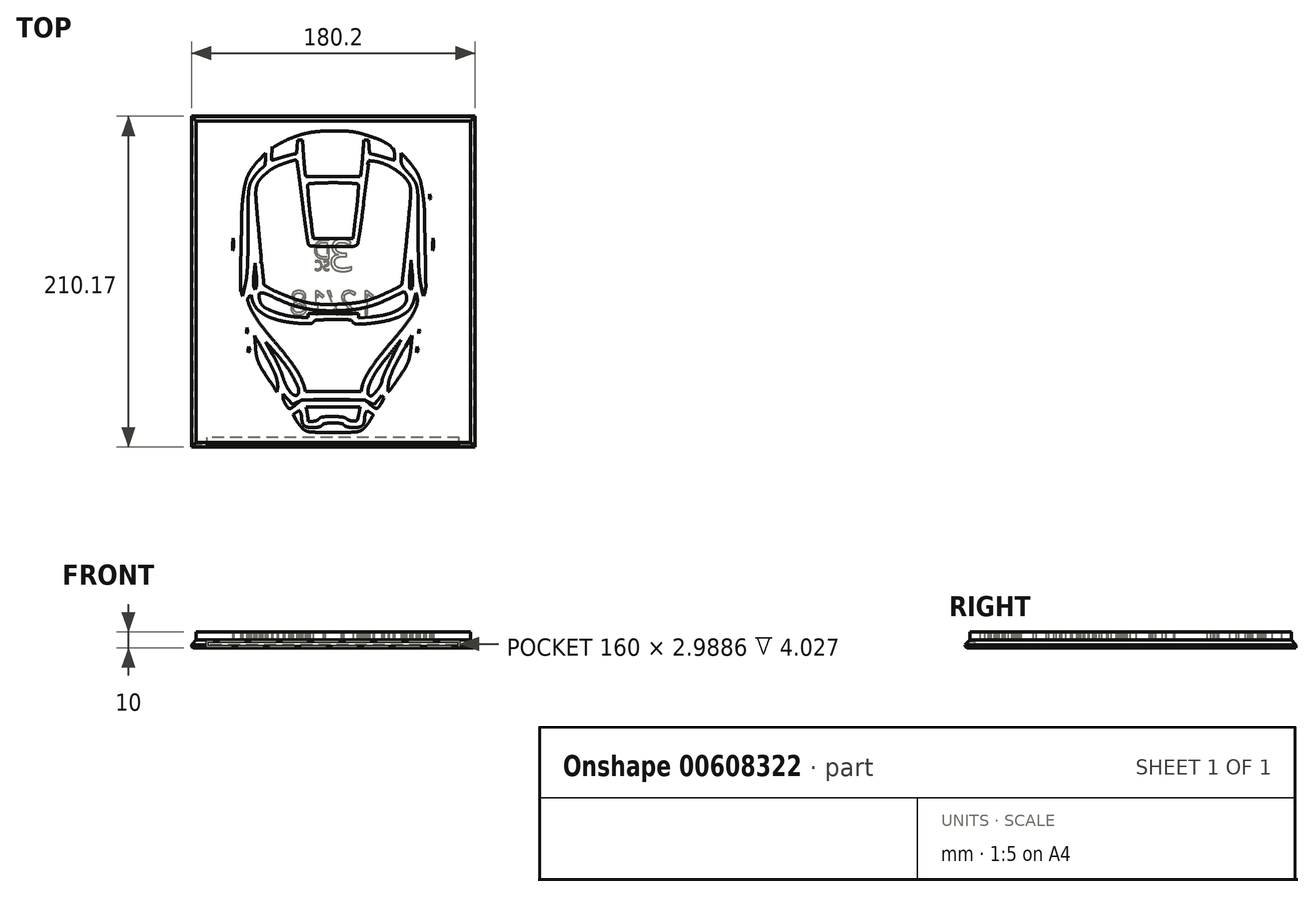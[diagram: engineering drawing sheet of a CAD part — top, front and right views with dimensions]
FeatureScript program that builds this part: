
annotation { "Feature Type Name" : "Feature", "Feature Type Description" : "" }
export const myFeature = defineFeature(function(context is Context, id is Id, definition is map)
    precondition{}
    {
        {
            var Q0;
            Q0=qCreatedBy(makeId("Top.planeOp"),FACE);
            var sketch = newSketch(context, id + "F0", { "sketchPlane" : qUnion([Q0])});
            skLineSegment(sketch, "E0.bottom", {"start": v(-90, 105) * mm, "end": v(90, 105) * mm});
            skLineSegment(sketch, "E0.top", {"start": v(-90, -105) * mm, "end": v(90, -105) * mm});
            skLineSegment(sketch, "E0.left", {"start": v(-90, 105) * mm, "end": v(-90, -105) * mm});
            skLineSegment(sketch, "E0.right", {"start": v(90, 105) * mm, "end": v(90, -105) * mm});
            skSolve(sketch);
        }
        {
            var Q0;
            Q0=makeQuery(id+"F0.imprint","IMPRINT",FACE,{"disambiguationData":[TD([[makeQuery(id+"F0.imprint","IMPRINT",EDGE,{"derivedFrom":sQuery(id+"F0.wireOp",EDGE,"E0.bottom")}),-1.0]])]});
            extrude(context, id + "F1", {"entities" : qUnion([Q0]), "depth" : 5 * mm, "offsetDistance" : 25 * mm, "hasDraft" : true, "draftAngle" : 3 * degree});
        }
        {
            var Q0;
            Q0=makeQuery(id+"F1.opExtrude","CAP_EDGE",EDGE,{"disambiguationData":[OSD([sQuery(id+"F0.wireOp",EDGE,"E0.left")])],"isStart":false});
            var Q1;
            Q1=makeQuery(id+"F1.opExtrude","CAP_EDGE",EDGE,{"disambiguationData":[OSD([sQuery(id+"F0.wireOp",EDGE,"E0.bottom")])],"isStart":false});
            var Q2;
            Q2=makeQuery(id+"F1.opExtrude","CAP_EDGE",EDGE,{"disambiguationData":[OSD([sQuery(id+"F0.wireOp",EDGE,"E0.right")])],"isStart":false});
            var Q3;
            Q3=makeQuery(id+"F1.opExtrude","CAP_EDGE",EDGE,{"disambiguationData":[OSD([sQuery(id+"F0.wireOp",EDGE,"E0.top")])],"isStart":false});
            chamfer(context, id + "F2", {"entities" : qUnion([Q0, Q1, Q2, Q3]), "width" : 3 * mm, "tangentPropagation" : true});
        }
        {
            var Q0;
            Q0=makeQuery(id+"F1.opExtrude","CAP_EDGE",EDGE,{"disambiguationData":[OSD([sQuery(id+"F0.wireOp",EDGE,"E0.right")])],"isStart":true});
            var Q1;
            {var subQ0=sQuery(id+"F0.wireOp",EDGE,"E0.bottom");Q1=makeQuery(id+"F2.opChamfer","BLEND_EDGE",EDGE,{"blendedFrom":[makeQuery(id+"F1.opExtrude","CAP_EDGE",EDGE,{"disambiguationData":[OSD([subQ0])],"isStart":false}),makeQuery(id+"F1.opExtrude","SWEPT_FACE",FACE,{"disambiguationData":[OSD([subQ0])]})],"blendedInto":[makeQuery(id+"F1.opExtrude","SWEPT_FACE",FACE,{"disambiguationData":[OSD([subQ0])]})]});}
            var Q2;
            Q2=makeQuery(id+"F1.opExtrude","CAP_EDGE",EDGE,{"disambiguationData":[OSD([sQuery(id+"F0.wireOp",EDGE,"E0.left")])],"isStart":true});
            var Q3;
            Q3=makeQuery(id+"F1.opExtrude","CAP_EDGE",EDGE,{"disambiguationData":[OSD([sQuery(id+"F0.wireOp",EDGE,"E0.top")])],"isStart":true});
            chamfer(context, id + "F3", {"entities" : qUnion([Q0, Q1, Q2, Q3]), "width" : 1 * mm, "tangentPropagation" : true});
        }
        {
            var Q0;
            Q0=makeQuery(id+"F1.opExtrude","CAP_FACE",FACE,{"disambiguationData":[OSD([sQuery(id+"F0.wireOp",EDGE,"E0.bottom"),sQuery(id+"F0.wireOp",EDGE,"E0.top"),sQuery(id+"F0.wireOp",EDGE,"E0.left"),sQuery(id+"F0.wireOp",EDGE,"E0.right")])],"isStart":true});
            var sketch = newSketch(context, id + "F4", { "sketchPlane" : qUnion([Q0])});
            skText(sketch, "E1", { "text": "D", "fontName": "OpenSans-Regular.ttf"});
            skText(sketch, "E2", { "text": "S", "fontName": "OpenSans-Regular.ttf"});
            skLineSegment(sketch, "E3", {"start": v(17.22, -16.7) * mm, "end": v(-3.14, -16.7) * mm, "construction": true});
            skText(sketch, "E4", { "text": "3", "fontName": "OpenSans-Regular.ttf"});
            skText(sketch, "E5", { "text": "C", "fontName": "OpenSans-Regular.ttf"});
            skText(sketch, "E6", { "text": "12/18", "fontName": "OpenSans-Regular.ttf"});
            const initialGuessF4  = {"E1": [-0.001, -0.01442, -1, 0, 0.0118], "E2": [-0.00213, -0.0072, -1, 0, 0.006], "E4": [0.01283, -0.0067, -1, 0, 0.02], "E5": [-0.00664, -0.0072, -1, 0, 0.006], "E6": [0.02743, 0.0209, -1, 0, 0.015]};
            skSetInitialGuess(sketch, initialGuessF4);
            skSolve(sketch);
        }
        {
            var Q0;
            Q0 = qSketchRegion(id + "F4", true);
            extrude(context, id + "F5", {"entities" : qUnion([Q0]), "operationType" : NewBodyOperationType.REMOVE, "flatOperationType" : FlatOperationType.REMOVE, "oppositeDirection" : true, "depth" : 0.5 * mm, "offsetDistance" : 25 * mm, "domain" : OperationDomain.MODEL});
        }
        {
            var Q0;
            Q0=makeQuery(id+"F1.opExtrude","CAP_FACE",FACE,{"disambiguationData":[OSD([sQuery(id+"F0.wireOp",EDGE,"E0.bottom"),sQuery(id+"F0.wireOp",EDGE,"E0.top"),sQuery(id+"F0.wireOp",EDGE,"E0.left"),sQuery(id+"F0.wireOp",EDGE,"E0.right")])],"isStart":false});
            var sketch = newSketch(context, id + "F6", { "sketchPlane" : qUnion([Q0])});
            skArc(sketch, "E7", {"start": v(-19.82, -98.53) * mm, "mid": v(-21.11, -97.69) * mm, "end": v(-22.15, -96.55) * mm});
            skArc(sketch, "E8", {"start": v(-22.15, -96.55) * mm, "mid": v(-28.55, -87.41) * mm, "end": v(-34.94, -78.26) * mm});
            skArc(sketch, "E9", {"start": v(-34.94, -78.26) * mm, "mid": v(-40.82, -69.73) * mm, "end": v(-46.64, -61.17) * mm});
            skArc(sketch, "E10", {"start": v(-46.64, -61.17) * mm, "mid": v(-49.1, -57.28) * mm, "end": v(-51.3, -53.25) * mm});
            skArc(sketch, "E11", {"start": v(-51.3, -53.25) * mm, "mid": v(-51.72, -52.27) * mm, "end": v(-52, -51.23) * mm});
            skArc(sketch, "E12", {"start": v(-52, -51.23) * mm, "mid": v(-52.4, -49.18) * mm, "end": v(-52.74, -47.12) * mm});
            skArc(sketch, "E13", {"start": v(-52.74, -47.12) * mm, "mid": v(-53.12, -44.5) * mm, "end": v(-53.44, -41.9) * mm});
            skArc(sketch, "E14", {"start": v(-53.44, -41.9) * mm, "mid": v(-53.76, -38.83) * mm, "end": v(-54.03, -35.75) * mm});
            skArc(sketch, "E15", {"start": v(-54.03, -35.75) * mm, "mid": v(-54.3, -32.88) * mm, "end": v(-54.6, -30.02) * mm});
            skArc(sketch, "E16", {"start": v(-54.6, -30.02) * mm, "mid": v(-54.9, -27.4) * mm, "end": v(-55.27, -24.78) * mm});
            skArc(sketch, "E17", {"start": v(-55.27, -24.78) * mm, "mid": v(-55.6, -22.6) * mm, "end": v(-55.98, -20.43) * mm});
            skArc(sketch, "E18", {"start": v(-55.98, -20.43) * mm, "mid": v(-56.2, -19.57) * mm, "end": v(-56.55, -18.75) * mm});
            skArc(sketch, "E19", {"start": v(-56.55, -18.75) * mm, "mid": v(-56.9, -18.1) * mm, "end": v(-57.23, -17.46) * mm});
            skArc(sketch, "E20", {"start": v(-57.23, -17.46) * mm, "mid": v(-57.75, -16.49) * mm, "end": v(-58.27, -15.52) * mm});
            skArc(sketch, "E21", {"start": v(-58.27, -15.52) * mm, "mid": v(-58.85, -14.44) * mm, "end": v(-59.43, -13.35) * mm});
            skArc(sketch, "E22", {"start": v(-59.43, -13.35) * mm, "mid": v(-60, -12.3) * mm, "end": v(-60.56, -11.25) * mm});
            skArc(sketch, "E23", {"start": v(-60.56, -11.25) * mm, "mid": v(-61.46, -9.37) * mm, "end": v(-62.14, -7.4) * mm});
            skArc(sketch, "E24", {"start": v(-62.14, -7.4) * mm, "mid": v(-62.6, -5.37) * mm, "end": v(-62.85, -3.32) * mm});
            skArc(sketch, "E25", {"start": v(-62.85, -3.32) * mm, "mid": v(-62.99, 0.04) * mm, "end": v(-63, 3.4) * mm});
            skArc(sketch, "E26", {"start": v(-63, 3.4) * mm, "mid": v(-62.83, 12.82) * mm, "end": v(-62.63, 22.25) * mm});
            skArc(sketch, "E27", {"start": v(-62.63, 22.25) * mm, "mid": v(-62.36, 32.9) * mm, "end": v(-62, 43.55) * mm});
            skArc(sketch, "E28", {"start": v(-62, 43.55) * mm, "mid": v(-61.67, 49.6) * mm, "end": v(-61.11, 55.62) * mm});
            skArc(sketch, "E29", {"start": v(-61.11, 55.62) * mm, "mid": v(-60.53, 59.69) * mm, "end": v(-59.7, 63.71) * mm});
            skArc(sketch, "E30", {"start": v(-59.7, 63.71) * mm, "mid": v(-58.7, 67.02) * mm, "end": v(-57.37, 70.2) * mm});
            skArc(sketch, "E31", {"start": v(-57.37, 70.2) * mm, "mid": v(-55.63, 73.3) * mm, "end": v(-53.57, 76.2) * mm});
            skArc(sketch, "E32", {"start": v(-53.57, 76.2) * mm, "mid": v(-50.88, 79.31) * mm, "end": v(-47.97, 82.23) * mm});
            skArc(sketch, "E33", {"start": v(-47.97, 82.23) * mm, "mid": v(-44.7, 85.08) * mm, "end": v(-41.22, 87.7) * mm});
            skArc(sketch, "E34", {"start": v(-41.22, 87.7) * mm, "mid": v(-37.66, 90.02) * mm, "end": v(-33.93, 92.06) * mm});
            skArc(sketch, "E35", {"start": v(-33.93, 92.06) * mm, "mid": v(-29.7, 94.07) * mm, "end": v(-25.37, 95.89) * mm});
            skArc(sketch, "E36", {"start": v(-25.37, 95.89) * mm, "mid": v(-21.73, 97.17) * mm, "end": v(-18, 98.16) * mm});
            skArc(sketch, "E37", {"start": v(-18, 98.16) * mm, "mid": v(-14.09, 98.9) * mm, "end": v(-10.14, 99.33) * mm});
            skArc(sketch, "E38", {"start": v(-10.14, 99.33) * mm, "mid": v(-5.1, 99.6) * mm, "end": v(-0.06, 99.7) * mm});
            skArc(sketch, "E39", {"start": v(-0.06, 99.7) * mm, "mid": v(4.99, 99.6) * mm, "end": v(10.03, 99.33) * mm});
            skArc(sketch, "E40", {"start": v(10.03, 99.33) * mm, "mid": v(13.97, 98.9) * mm, "end": v(17.88, 98.16) * mm});
            skArc(sketch, "E41", {"start": v(17.88, 98.16) * mm, "mid": v(21.61, 97.17) * mm, "end": v(25.26, 95.89) * mm});
            skArc(sketch, "E42", {"start": v(25.26, 95.89) * mm, "mid": v(29.58, 94.07) * mm, "end": v(33.82, 92.06) * mm});
            skArc(sketch, "E43", {"start": v(33.82, 92.06) * mm, "mid": v(37.54, 90.02) * mm, "end": v(41.1, 87.71) * mm});
            skArc(sketch, "E44", {"start": v(41.1, 87.71) * mm, "mid": v(44.57, 85.09) * mm, "end": v(47.85, 82.23) * mm});
            skArc(sketch, "E45", {"start": v(47.85, 82.23) * mm, "mid": v(50.76, 79.32) * mm, "end": v(53.45, 76.2) * mm});
            skArc(sketch, "E46", {"start": v(53.45, 76.2) * mm, "mid": v(55.53, 73.3) * mm, "end": v(57.27, 70.2) * mm});
            skArc(sketch, "E47", {"start": v(57.27, 70.2) * mm, "mid": v(58.6, 67.01) * mm, "end": v(59.57, 63.7) * mm});
            skArc(sketch, "E48", {"start": v(59.57, 63.7) * mm, "mid": v(60.41, 59.49) * mm, "end": v(61, 55.23) * mm});
            skArc(sketch, "E49", {"start": v(61, 55.23) * mm, "mid": v(61.57, 48.95) * mm, "end": v(61.91, 42.65) * mm});
            skArc(sketch, "E50", {"start": v(61.91, 42.65) * mm, "mid": v(62.28, 31.97) * mm, "end": v(62.55, 21.28) * mm});
            skArc(sketch, "E51", {"start": v(62.55, 21.28) * mm, "mid": v(62.74, 12.18) * mm, "end": v(62.9, 3.07) * mm});
            skArc(sketch, "E52", {"start": v(62.9, 3.07) * mm, "mid": v(62.88, -0.18) * mm, "end": v(62.74, -3.44) * mm});
            skArc(sketch, "E53", {"start": v(62.74, -3.44) * mm, "mid": v(62.5, -5.45) * mm, "end": v(62.03, -7.42) * mm});
            skArc(sketch, "E54", {"start": v(62.03, -7.42) * mm, "mid": v(61.34, -9.38) * mm, "end": v(60.45, -11.25) * mm});
            skArc(sketch, "E55", {"start": v(60.45, -11.25) * mm, "mid": v(59.89, -12.3) * mm, "end": v(59.32, -13.35) * mm});
            skArc(sketch, "E56", {"start": v(59.32, -13.35) * mm, "mid": v(58.74, -14.44) * mm, "end": v(58.16, -15.52) * mm});
            skArc(sketch, "E57", {"start": v(58.16, -15.52) * mm, "mid": v(57.64, -16.49) * mm, "end": v(57.12, -17.46) * mm});
            skArc(sketch, "E58", {"start": v(57.12, -17.46) * mm, "mid": v(56.78, -18.1) * mm, "end": v(56.44, -18.75) * mm});
            skArc(sketch, "E59", {"start": v(56.44, -18.75) * mm, "mid": v(56.09, -19.57) * mm, "end": v(55.86, -20.43) * mm});
            skArc(sketch, "E60", {"start": v(55.86, -20.43) * mm, "mid": v(55.5, -22.6) * mm, "end": v(55.16, -24.78) * mm});
            skArc(sketch, "E61", {"start": v(55.16, -24.78) * mm, "mid": v(54.8, -27.4) * mm, "end": v(54.48, -30.02) * mm});
            skArc(sketch, "E62", {"start": v(54.48, -30.02) * mm, "mid": v(54.18, -32.88) * mm, "end": v(53.92, -35.75) * mm});
            skArc(sketch, "E63", {"start": v(53.92, -35.75) * mm, "mid": v(53.64, -38.83) * mm, "end": v(53.32, -41.9) * mm});
            skArc(sketch, "E64", {"start": v(53.32, -41.9) * mm, "mid": v(53, -44.5) * mm, "end": v(52.63, -47.12) * mm});
            skArc(sketch, "E65", {"start": v(52.63, -47.12) * mm, "mid": v(52.28, -49.18) * mm, "end": v(51.9, -51.23) * mm});
            skArc(sketch, "E66", {"start": v(51.9, -51.23) * mm, "mid": v(51.6, -52.27) * mm, "end": v(51.19, -53.25) * mm});
            skArc(sketch, "E67", {"start": v(51.19, -53.25) * mm, "mid": v(50.64, -54.26) * mm, "end": v(50.05, -55.24) * mm});
            skArc(sketch, "E68", {"start": v(50.05, -55.24) * mm, "mid": v(48.05, -58.33) * mm, "end": v(46.05, -61.42) * mm});
            skArc(sketch, "E69", {"start": v(46.05, -61.42) * mm, "mid": v(43.65, -65.08) * mm, "end": v(41.24, -68.73) * mm});
            skArc(sketch, "E70", {"start": v(41.24, -68.73) * mm, "mid": v(38.54, -72.79) * mm, "end": v(35.83, -76.83) * mm});
            skArc(sketch, "E71", {"start": v(35.83, -76.83) * mm, "mid": v(32.8, -81.28) * mm, "end": v(29.75, -85.71) * mm});
            skArc(sketch, "E72", {"start": v(29.75, -85.71) * mm, "mid": v(27.37, -89.06) * mm, "end": v(24.92, -92.37) * mm});
            skArc(sketch, "E73", {"start": v(24.92, -92.37) * mm, "mid": v(23.03, -94.84) * mm, "end": v(21.1, -97.28) * mm});
            skArc(sketch, "E74", {"start": v(21.1, -97.28) * mm, "mid": v(20.33, -98.03) * mm, "end": v(19.42, -98.58) * mm});
            skArc(sketch, "E75", {"start": v(19.42, -98.58) * mm, "mid": v(17.28, -99.3) * mm, "end": v(15.03, -99.58) * mm});
            skArc(sketch, "E76", {"start": v(15.03, -99.58) * mm, "mid": v(7.38, -99.68) * mm, "end": v(-0.26, -99.7) * mm});
            skArc(sketch, "E77", {"start": v(-0.26, -99.7) * mm, "mid": v(-7.93, -99.65) * mm, "end": v(-15.6, -99.54) * mm});
            skArc(sketch, "E78", {"start": v(-15.6, -99.54) * mm, "mid": v(-17.76, -99.26) * mm, "end": v(-19.82, -98.53) * mm});
            skArc(sketch, "E79", {"start": v(19.8, -92.91) * mm, "mid": v(20.36, -92.28) * mm, "end": v(20.92, -91.62) * mm});
            skArc(sketch, "E80", {"start": v(20.92, -91.62) * mm, "mid": v(21.52, -90.87) * mm, "end": v(22.1, -90.1) * mm});
            skArc(sketch, "E81", {"start": v(22.1, -90.1) * mm, "mid": v(22.64, -89.34) * mm, "end": v(23.16, -88.57) * mm});
            skArc(sketch, "E82", {"start": v(23.16, -88.57) * mm, "mid": v(24.32, -86.59) * mm, "end": v(25.39, -84.55) * mm});
            skLineSegment(sketch, "E83", {"start": v(25.39, -84.55) * mm, "end": v(23.48, -83.15) * mm});
            skLineSegment(sketch, "E84", {"start": v(23.48, -83.15) * mm, "end": v(21.56, -81.75) * mm});
            skLineSegment(sketch, "E85", {"start": v(21.56, -81.75) * mm, "end": v(20.77, -83) * mm});
            skArc(sketch, "E86", {"start": v(20.77, -83) * mm, "mid": v(20.6, -83.32) * mm, "end": v(20.46, -83.65) * mm});
            skArc(sketch, "E87", {"start": v(20.46, -83.65) * mm, "mid": v(20.32, -84.1) * mm, "end": v(20.2, -84.57) * mm});
            skArc(sketch, "E88", {"start": v(20.2, -84.57) * mm, "mid": v(20.1, -85.08) * mm, "end": v(20.02, -85.6) * mm});
            skArc(sketch, "E89", {"start": v(20.02, -85.6) * mm, "mid": v(19.98, -86.08) * mm, "end": v(19.96, -86.57) * mm});
            skArc(sketch, "E90", {"start": v(19.96, -86.57) * mm, "mid": v(19.86, -88.07) * mm, "end": v(19.57, -89.54) * mm});
            skArc(sketch, "E91", {"start": v(19.57, -89.54) * mm, "mid": v(19.14, -90.56) * mm, "end": v(18.44, -91.41) * mm});
            skArc(sketch, "E92", {"start": v(18.44, -91.41) * mm, "mid": v(17.47, -92.07) * mm, "end": v(16.37, -92.44) * mm});
            skArc(sketch, "E93", {"start": v(16.37, -92.44) * mm, "mid": v(14.7, -92.67) * mm, "end": v(13.03, -92.75) * mm});
            skArc(sketch, "E94", {"start": v(13.03, -92.75) * mm, "mid": v(11.96, -92.73) * mm, "end": v(10.9, -92.66) * mm});
            skArc(sketch, "E95", {"start": v(10.9, -92.66) * mm, "mid": v(10, -92.54) * mm, "end": v(9.13, -92.36) * mm});
            skArc(sketch, "E96", {"start": v(9.13, -92.36) * mm, "mid": v(8.44, -92.16) * mm, "end": v(7.78, -91.9) * mm});
            skArc(sketch, "E97", {"start": v(7.78, -91.9) * mm, "mid": v(7.32, -91.62) * mm, "end": v(6.94, -91.25) * mm});
            skArc(sketch, "E98", {"start": v(6.94, -91.25) * mm, "mid": v(6.54, -90.87) * mm, "end": v(6.05, -90.59) * mm});
            skArc(sketch, "E99", {"start": v(6.05, -90.59) * mm, "mid": v(5.33, -90.32) * mm, "end": v(4.59, -90.12) * mm});
            skArc(sketch, "E100", {"start": v(4.59, -90.12) * mm, "mid": v(3.59, -89.95) * mm, "end": v(2.58, -89.84) * mm});
            skArc(sketch, "E101", {"start": v(2.58, -89.84) * mm, "mid": v(1.26, -89.78) * mm, "end": v(-0.06, -89.75) * mm});
            skArc(sketch, "E102", {"start": v(-0.06, -89.75) * mm, "mid": v(-1.37, -89.78) * mm, "end": v(-2.7, -89.84) * mm});
            skArc(sketch, "E103", {"start": v(-2.7, -89.84) * mm, "mid": v(-3.7, -89.95) * mm, "end": v(-4.7, -90.12) * mm});
            skArc(sketch, "E104", {"start": v(-4.7, -90.12) * mm, "mid": v(-5.44, -90.32) * mm, "end": v(-6.16, -90.59) * mm});
            skArc(sketch, "E105", {"start": v(-6.16, -90.59) * mm, "mid": v(-6.65, -90.87) * mm, "end": v(-7.06, -91.25) * mm});
            skArc(sketch, "E106", {"start": v(-7.06, -91.25) * mm, "mid": v(-7.44, -91.62) * mm, "end": v(-7.9, -91.9) * mm});
            skArc(sketch, "E107", {"start": v(-7.9, -91.9) * mm, "mid": v(-8.55, -92.16) * mm, "end": v(-9.24, -92.36) * mm});
            skArc(sketch, "E108", {"start": v(-9.24, -92.36) * mm, "mid": v(-10.12, -92.54) * mm, "end": v(-11, -92.66) * mm});
            skArc(sketch, "E109", {"start": v(-11, -92.66) * mm, "mid": v(-12.07, -92.73) * mm, "end": v(-13.14, -92.75) * mm});
            skArc(sketch, "E110", {"start": v(-13.14, -92.75) * mm, "mid": v(-14.82, -92.67) * mm, "end": v(-16.48, -92.44) * mm});
            skArc(sketch, "E111", {"start": v(-16.48, -92.44) * mm, "mid": v(-17.58, -92.07) * mm, "end": v(-18.55, -91.41) * mm});
            skArc(sketch, "E112", {"start": v(-18.55, -91.41) * mm, "mid": v(-19.26, -90.56) * mm, "end": v(-19.69, -89.54) * mm});
            skArc(sketch, "E113", {"start": v(-19.69, -89.54) * mm, "mid": v(-19.97, -88.07) * mm, "end": v(-20.07, -86.57) * mm});
            skArc(sketch, "E114", {"start": v(-20.07, -86.57) * mm, "mid": v(-20.09, -86.08) * mm, "end": v(-20.14, -85.6) * mm});
            skArc(sketch, "E115", {"start": v(-20.14, -85.6) * mm, "mid": v(-20.21, -85.08) * mm, "end": v(-20.32, -84.57) * mm});
            skArc(sketch, "E116", {"start": v(-20.32, -84.57) * mm, "mid": v(-20.43, -84.1) * mm, "end": v(-20.57, -83.65) * mm});
            skArc(sketch, "E117", {"start": v(-20.57, -83.65) * mm, "mid": v(-21.07, -82.67) * mm, "end": v(-21.67, -81.75) * mm});
            skLineSegment(sketch, "E118", {"start": v(-21.67, -81.75) * mm, "end": v(-23.59, -83.15) * mm});
            skLineSegment(sketch, "E119", {"start": v(-23.59, -83.15) * mm, "end": v(-25.5, -84.55) * mm});
            skLineSegment(sketch, "E120", {"start": v(-25.5, -84.55) * mm, "end": v(-24.03, -87.31) * mm});
            skArc(sketch, "E121", {"start": v(-24.03, -87.31) * mm, "mid": v(-23.67, -87.95) * mm, "end": v(-23.28, -88.57) * mm});
            skArc(sketch, "E122", {"start": v(-23.28, -88.57) * mm, "mid": v(-22.75, -89.34) * mm, "end": v(-22.21, -90.1) * mm});
            skArc(sketch, "E123", {"start": v(-22.21, -90.1) * mm, "mid": v(-21.63, -90.87) * mm, "end": v(-21.03, -91.62) * mm});
            skArc(sketch, "E124", {"start": v(-21.03, -91.62) * mm, "mid": v(-20.48, -92.28) * mm, "end": v(-19.9, -92.91) * mm});
            skArc(sketch, "E125", {"start": v(-19.9, -92.91) * mm, "mid": v(-18.91, -93.83) * mm, "end": v(-17.8, -94.59) * mm});
            skArc(sketch, "E126", {"start": v(-17.8, -94.59) * mm, "mid": v(-16.65, -95.1) * mm, "end": v(-15.44, -95.4) * mm});
            skArc(sketch, "E127", {"start": v(-15.44, -95.4) * mm, "mid": v(-13.44, -95.62) * mm, "end": v(-11.43, -95.7) * mm});
            skArc(sketch, "E128", {"start": v(-11.43, -95.7) * mm, "mid": v(-5.75, -95.74) * mm, "end": v(-0.06, -95.75) * mm});
            skArc(sketch, "E129", {"start": v(-0.06, -95.75) * mm, "mid": v(5.63, -95.74) * mm, "end": v(11.32, -95.7) * mm});
            skArc(sketch, "E130", {"start": v(11.32, -95.7) * mm, "mid": v(13.33, -95.62) * mm, "end": v(15.32, -95.4) * mm});
            skArc(sketch, "E131", {"start": v(15.32, -95.4) * mm, "mid": v(16.54, -95.1) * mm, "end": v(17.68, -94.59) * mm});
            skArc(sketch, "E132", {"start": v(17.68, -94.59) * mm, "mid": v(18.8, -93.83) * mm, "end": v(19.8, -92.91) * mm});
            skArc(sketch, "E133", {"start": v(-9.06, -87.25) * mm, "mid": v(-8, -86.39) * mm, "end": v(-6.68, -86) * mm});
            skArc(sketch, "E134", {"start": v(-6.68, -86) * mm, "mid": v(-3.67, -85.77) * mm, "end": v(-0.65, -85.7) * mm});
            skArc(sketch, "E135", {"start": v(-0.65, -85.7) * mm, "mid": v(2.38, -85.77) * mm, "end": v(5.4, -86) * mm});
            skArc(sketch, "E136", {"start": v(5.4, -86) * mm, "mid": v(7.04, -86.4) * mm, "end": v(8.5, -87.22) * mm});
            skArc(sketch, "E137", {"start": v(8.5, -87.22) * mm, "mid": v(9.34, -87.76) * mm, "end": v(10.25, -88.17) * mm});
            skArc(sketch, "E138", {"start": v(10.25, -88.17) * mm, "mid": v(11.3, -88.48) * mm, "end": v(12.39, -88.67) * mm});
            skArc(sketch, "E139", {"start": v(12.39, -88.67) * mm, "mid": v(13.34, -88.72) * mm, "end": v(14.3, -88.65) * mm});
            skArc(sketch, "E140", {"start": v(14.3, -88.65) * mm, "mid": v(14.85, -88.44) * mm, "end": v(15.25, -88) * mm});
            skArc(sketch, "E141", {"start": v(15.25, -88) * mm, "mid": v(15.37, -87.77) * mm, "end": v(15.46, -87.52) * mm});
            skArc(sketch, "E142", {"start": v(15.46, -87.52) * mm, "mid": v(15.6, -86.95) * mm, "end": v(15.75, -86.37) * mm});
            skArc(sketch, "E143", {"start": v(15.75, -86.37) * mm, "mid": v(15.92, -85.69) * mm, "end": v(16.07, -85) * mm});
            skArc(sketch, "E144", {"start": v(16.07, -85) * mm, "mid": v(16.57, -82.38) * mm, "end": v(17.03, -79.75) * mm});
            skLineSegment(sketch, "E145", {"start": v(17.03, -79.75) * mm, "end": v(-0.14, -79.75) * mm});
            skLineSegment(sketch, "E146", {"start": v(-0.14, -79.75) * mm, "end": v(-17.3, -79.75) * mm});
            skLineSegment(sketch, "E147", {"start": v(-17.3, -79.75) * mm, "end": v(-16.68, -82.88) * mm});
            skArc(sketch, "E148", {"start": v(-16.68, -82.88) * mm, "mid": v(-16.56, -83.53) * mm, "end": v(-16.44, -84.18) * mm});
            skArc(sketch, "E149", {"start": v(-16.44, -84.18) * mm, "mid": v(-16.34, -84.83) * mm, "end": v(-16.24, -85.49) * mm});
            skArc(sketch, "E150", {"start": v(-16.24, -85.49) * mm, "mid": v(-16.16, -86.07) * mm, "end": v(-16.1, -86.65) * mm});
            skArc(sketch, "E151", {"start": v(-16.1, -86.65) * mm, "mid": v(-16.05, -87.7) * mm, "end": v(-16.06, -88.75) * mm});
            skLineSegment(sketch, "E152", {"start": v(-16.06, -88.75) * mm, "end": v(-13.18, -88.75) * mm});
            skArc(sketch, "E153", {"start": v(-13.18, -88.75) * mm, "mid": v(-12.58, -88.73) * mm, "end": v(-11.99, -88.64) * mm});
            skArc(sketch, "E154", {"start": v(-11.99, -88.64) * mm, "mid": v(-11.38, -88.5) * mm, "end": v(-10.78, -88.31) * mm});
            skArc(sketch, "E155", {"start": v(-10.78, -88.31) * mm, "mid": v(-10.25, -88.1) * mm, "end": v(-9.74, -87.83) * mm});
            skArc(sketch, "E156", {"start": v(-9.74, -87.83) * mm, "mid": v(-9.37, -87.57) * mm, "end": v(-9.06, -87.25) * mm});
            skLineSegment(sketch, "E157", {"start": v(-23.56, -78.17) * mm, "end": v(-20.56, -75.66) * mm});
            skLineSegment(sketch, "E158", {"start": v(-20.56, -75.66) * mm, "end": v(-23.21, -76.82) * mm});
            skLineSegment(sketch, "E159", {"start": v(-23.21, -76.82) * mm, "end": v(-25.87, -78) * mm});
            skLineSegment(sketch, "E160", {"start": v(-25.87, -78) * mm, "end": v(-28.94, -74.62) * mm});
            skLineSegment(sketch, "E161", {"start": v(-28.94, -74.62) * mm, "end": v(-32, -71.25) * mm});
            skLineSegment(sketch, "E162", {"start": v(-32, -71.25) * mm, "end": v(-32.03, -73.1) * mm});
            skArc(sketch, "E163", {"start": v(-32.03, -73.1) * mm, "mid": v(-31.94, -74.13) * mm, "end": v(-31.65, -75.13) * mm});
            skArc(sketch, "E164", {"start": v(-31.65, -75.13) * mm, "mid": v(-31.04, -76.5) * mm, "end": v(-30.34, -77.8) * mm});
            skArc(sketch, "E165", {"start": v(-30.34, -77.8) * mm, "mid": v(-29.58, -79.01) * mm, "end": v(-28.75, -80.17) * mm});
            skArc(sketch, "E166", {"start": v(-28.75, -80.17) * mm, "mid": v(-28.24, -80.58) * mm, "end": v(-27.6, -80.72) * mm});
            skArc(sketch, "E167", {"start": v(-27.6, -80.72) * mm, "mid": v(-27.3, -80.67) * mm, "end": v(-27.02, -80.56) * mm});
            skArc(sketch, "E168", {"start": v(-27.02, -80.56) * mm, "mid": v(-26.5, -80.27) * mm, "end": v(-25.98, -79.95) * mm});
            skArc(sketch, "E169", {"start": v(-25.98, -79.95) * mm, "mid": v(-25.37, -79.56) * mm, "end": v(-24.78, -79.13) * mm});
            skArc(sketch, "E170", {"start": v(-24.78, -79.13) * mm, "mid": v(-24.16, -78.66) * mm, "end": v(-23.56, -78.17) * mm});
            skLineSegment(sketch, "E171", {"start": v(30.5, -77.3) * mm, "end": v(32.36, -73.83) * mm});
            skLineSegment(sketch, "E172", {"start": v(32.36, -73.83) * mm, "end": v(31.56, -73.04) * mm});
            skLineSegment(sketch, "E173", {"start": v(31.56, -73.04) * mm, "end": v(30.77, -72.25) * mm});
            skLineSegment(sketch, "E174", {"start": v(30.77, -72.25) * mm, "end": v(28.3, -75.13) * mm});
            skLineSegment(sketch, "E175", {"start": v(28.3, -75.13) * mm, "end": v(25.81, -78.02) * mm});
            skLineSegment(sketch, "E176", {"start": v(25.81, -78.02) * mm, "end": v(23.13, -76.84) * mm});
            skLineSegment(sketch, "E177", {"start": v(23.13, -76.84) * mm, "end": v(20.44, -75.66) * mm});
            skLineSegment(sketch, "E178", {"start": v(20.44, -75.66) * mm, "end": v(23.44, -78.17) * mm});
            skArc(sketch, "E179", {"start": v(23.44, -78.17) * mm, "mid": v(24.73, -79.2) * mm, "end": v(26.08, -80.15) * mm});
            skArc(sketch, "E180", {"start": v(26.08, -80.15) * mm, "mid": v(26.82, -80.47) * mm, "end": v(27.63, -80.52) * mm});
            skArc(sketch, "E181", {"start": v(27.63, -80.52) * mm, "mid": v(28.36, -80.27) * mm, "end": v(28.93, -79.75) * mm});
            skArc(sketch, "E182", {"start": v(28.93, -79.75) * mm, "mid": v(29.76, -78.55) * mm, "end": v(30.5, -77.3) * mm});
            skArc(sketch, "E183", {"start": v(10.2, -75) * mm, "mid": v(7.86, -74.95) * mm, "end": v(5.53, -74.9) * mm});
            skArc(sketch, "E184", {"start": v(5.53, -74.9) * mm, "mid": v(2.74, -74.88) * mm, "end": v(-0.06, -74.87) * mm});
            skArc(sketch, "E185", {"start": v(-0.06, -74.87) * mm, "mid": v(-2.85, -74.88) * mm, "end": v(-5.64, -74.9) * mm});
            skArc(sketch, "E186", {"start": v(-5.64, -74.9) * mm, "mid": v(-13.1, -75.08) * mm, "end": v(-20.56, -75.33) * mm});
            skLineSegment(sketch, "E187", {"start": v(-20.56, -75.33) * mm, "end": v(-0.06, -75.33) * mm});
            skLineSegment(sketch, "E188", {"start": v(-0.06, -75.33) * mm, "end": v(20.44, -75.33) * mm});
            skLineSegment(sketch, "E189", {"start": v(20.44, -75.33) * mm, "end": v(10.2, -75) * mm});
            skArc(sketch, "E190", {"start": v(-22.52, -71.69) * mm, "mid": v(-21.9, -69.83) * mm, "end": v(-22.16, -67.89) * mm});
            skArc(sketch, "E191", {"start": v(-22.16, -67.89) * mm, "mid": v(-23.74, -64.2) * mm, "end": v(-25.56, -60.62) * mm});
            skArc(sketch, "E192", {"start": v(-25.56, -60.62) * mm, "mid": v(-28.13, -56.3) * mm, "end": v(-31, -52.18) * mm});
            skArc(sketch, "E193", {"start": v(-31, -52.18) * mm, "mid": v(-36.82, -45.06) * mm, "end": v(-43, -38.25) * mm});
            skLineSegment(sketch, "E194", {"start": v(-43, -38.25) * mm, "end": v(-38.5, -46.25) * mm});
            skArc(sketch, "E195", {"start": v(-38.5, -46.25) * mm, "mid": v(-37.57, -47.98) * mm, "end": v(-36.66, -49.72) * mm});
            skArc(sketch, "E196", {"start": v(-36.66, -49.72) * mm, "mid": v(-35.73, -51.61) * mm, "end": v(-34.84, -53.52) * mm});
            skArc(sketch, "E197", {"start": v(-34.84, -53.52) * mm, "mid": v(-34.05, -55.3) * mm, "end": v(-33.29, -57.09) * mm});
            skArc(sketch, "E198", {"start": v(-33.29, -57.09) * mm, "mid": v(-32.78, -58.41) * mm, "end": v(-32.34, -59.75) * mm});
            skArc(sketch, "E199", {"start": v(-32.34, -59.75) * mm, "mid": v(-31.28, -62.8) * mm, "end": v(-30.01, -65.78) * mm});
            skArc(sketch, "E200", {"start": v(-30.01, -65.78) * mm, "mid": v(-28.72, -68.13) * mm, "end": v(-27.15, -70.3) * mm});
            skArc(sketch, "E201", {"start": v(-27.15, -70.3) * mm, "mid": v(-25.94, -71.47) * mm, "end": v(-24.49, -72.3) * mm});
            skArc(sketch, "E202", {"start": v(-24.49, -72.3) * mm, "mid": v(-23.39, -72.37) * mm, "end": v(-22.52, -71.69) * mm});
            skArc(sketch, "E203", {"start": v(27.87, -69.03) * mm, "mid": v(28.48, -68.24) * mm, "end": v(29.05, -67.43) * mm});
            skArc(sketch, "E204", {"start": v(29.05, -67.43) * mm, "mid": v(29.57, -66.6) * mm, "end": v(30.04, -65.72) * mm});
            skArc(sketch, "E205", {"start": v(30.04, -65.72) * mm, "mid": v(30.41, -64.94) * mm, "end": v(30.74, -64.15) * mm});
            skArc(sketch, "E206", {"start": v(30.74, -64.15) * mm, "mid": v(30.9, -63.6) * mm, "end": v(30.94, -63.02) * mm});
            skArc(sketch, "E207", {"start": v(30.94, -63.02) * mm, "mid": v(31.01, -62.29) * mm, "end": v(31.22, -61.59) * mm});
            skArc(sketch, "E208", {"start": v(31.22, -61.59) * mm, "mid": v(31.95, -59.77) * mm, "end": v(32.7, -57.96) * mm});
            skArc(sketch, "E209", {"start": v(32.7, -57.96) * mm, "mid": v(33.66, -55.8) * mm, "end": v(34.65, -53.66) * mm});
            skArc(sketch, "E210", {"start": v(34.65, -53.66) * mm, "mid": v(38.74, -45.43) * mm, "end": v(42.95, -37.25) * mm});
            skLineSegment(sketch, "E211", {"start": v(42.95, -37.25) * mm, "end": v(41.2, -39.37) * mm});
            skArc(sketch, "E212", {"start": v(41.2, -39.37) * mm, "mid": v(37.74, -43.56) * mm, "end": v(34.31, -47.77) * mm});
            skArc(sketch, "E213", {"start": v(34.31, -47.77) * mm, "mid": v(32.2, -50.44) * mm, "end": v(30.12, -53.16) * mm});
            skArc(sketch, "E214", {"start": v(30.12, -53.16) * mm, "mid": v(28.66, -55.2) * mm, "end": v(27.26, -57.28) * mm});
            skArc(sketch, "E215", {"start": v(27.26, -57.28) * mm, "mid": v(26.09, -59.19) * mm, "end": v(25, -61.15) * mm});
            skArc(sketch, "E216", {"start": v(25, -61.15) * mm, "mid": v(24.05, -63.06) * mm, "end": v(23.18, -65.01) * mm});
            skArc(sketch, "E217", {"start": v(23.18, -65.01) * mm, "mid": v(22.6, -66.57) * mm, "end": v(22.17, -68.18) * mm});
            skArc(sketch, "E218", {"start": v(22.17, -68.18) * mm, "mid": v(22, -69.38) * mm, "end": v(21.96, -70.6) * mm});
            skArc(sketch, "E219", {"start": v(21.96, -70.6) * mm, "mid": v(22.14, -71.4) * mm, "end": v(22.61, -72.09) * mm});
            skArc(sketch, "E220", {"start": v(22.61, -72.09) * mm, "mid": v(23.05, -72.4) * mm, "end": v(23.56, -72.6) * mm});
            skArc(sketch, "E221", {"start": v(23.56, -72.6) * mm, "mid": v(24.07, -72.6) * mm, "end": v(24.54, -72.42) * mm});
            skArc(sketch, "E222", {"start": v(24.54, -72.42) * mm, "mid": v(25.22, -71.96) * mm, "end": v(25.8, -71.4) * mm});
            skArc(sketch, "E223", {"start": v(25.8, -71.4) * mm, "mid": v(26.85, -70.23) * mm, "end": v(27.87, -69.03) * mm});
            skArc(sketch, "E224", {"start": v(-36.5, -59.97) * mm, "mid": v(-36.96, -58.71) * mm, "end": v(-37.5, -57.48) * mm});
            skArc(sketch, "E225", {"start": v(-37.5, -57.48) * mm, "mid": v(-38.43, -55.51) * mm, "end": v(-39.39, -53.56) * mm});
            skArc(sketch, "E226", {"start": v(-39.39, -53.56) * mm, "mid": v(-40.52, -51.33) * mm, "end": v(-41.68, -49.12) * mm});
            skArc(sketch, "E227", {"start": v(-41.68, -49.12) * mm, "mid": v(-45.85, -41.66) * mm, "end": v(-50.13, -34.25) * mm});
            skLineSegment(sketch, "E228", {"start": v(-50.13, -34.25) * mm, "end": v(-49.46, -41.75) * mm});
            skArc(sketch, "E229", {"start": v(-49.46, -41.75) * mm, "mid": v(-49.14, -44.57) * mm, "end": v(-48.7, -47.37) * mm});
            skArc(sketch, "E230", {"start": v(-48.7, -47.37) * mm, "mid": v(-48.2, -49.43) * mm, "end": v(-47.5, -51.42) * mm});
            skArc(sketch, "E231", {"start": v(-47.5, -51.42) * mm, "mid": v(-46.46, -53.63) * mm, "end": v(-45.25, -55.74) * mm});
            skArc(sketch, "E232", {"start": v(-45.25, -55.74) * mm, "mid": v(-40.47, -63.04) * mm, "end": v(-35.56, -70.25) * mm});
            skLineSegment(sketch, "E233", {"start": v(-35.56, -70.25) * mm, "end": v(-35.24, -67.47) * mm});
            skArc(sketch, "E234", {"start": v(-35.24, -67.47) * mm, "mid": v(-35.2, -66.78) * mm, "end": v(-35.22, -66.08) * mm});
            skArc(sketch, "E235", {"start": v(-35.22, -66.08) * mm, "mid": v(-35.33, -65.1) * mm, "end": v(-35.48, -64.12) * mm});
            skArc(sketch, "E236", {"start": v(-35.48, -64.12) * mm, "mid": v(-35.68, -63.05) * mm, "end": v(-35.92, -61.98) * mm});
            skArc(sketch, "E237", {"start": v(-35.92, -61.98) * mm, "mid": v(-36.19, -60.97) * mm, "end": v(-36.5, -59.97) * mm});
            skArc(sketch, "E238", {"start": v(18.67, -65.5) * mm, "mid": v(19.53, -62.9) * mm, "end": v(20.7, -60.43) * mm});
            skArc(sketch, "E239", {"start": v(20.7, -60.43) * mm, "mid": v(22.52, -57.26) * mm, "end": v(24.5, -54.2) * mm});
            skArc(sketch, "E240", {"start": v(24.5, -54.2) * mm, "mid": v(27.28, -50.3) * mm, "end": v(30.2, -46.52) * mm});
            skArc(sketch, "E241", {"start": v(30.2, -46.52) * mm, "mid": v(34.2, -41.62) * mm, "end": v(38.3, -36.78) * mm});
            skArc(sketch, "E242", {"start": v(38.3, -36.78) * mm, "mid": v(42.21, -32.12) * mm, "end": v(46, -27.35) * mm});
            skArc(sketch, "E243", {"start": v(46, -27.35) * mm, "mid": v(48.5, -23.9) * mm, "end": v(50.74, -20.28) * mm});
            skArc(sketch, "E244", {"start": v(50.74, -20.28) * mm, "mid": v(52.1, -17.58) * mm, "end": v(53.16, -14.76) * mm});
            skArc(sketch, "E245", {"start": v(53.16, -14.76) * mm, "mid": v(53.39, -10.97) * mm, "end": v(52.6, -7.25) * mm});
            skLineSegment(sketch, "E246", {"start": v(52.6, -7.25) * mm, "end": v(51.3, -11.65) * mm});
            skArc(sketch, "E247", {"start": v(51.3, -11.65) * mm, "mid": v(50.7, -13.43) * mm, "end": v(49.96, -15.16) * mm});
            skArc(sketch, "E248", {"start": v(49.96, -15.16) * mm, "mid": v(49.2, -16.52) * mm, "end": v(48.29, -17.78) * mm});
            skArc(sketch, "E249", {"start": v(48.29, -17.78) * mm, "mid": v(47.2, -18.9) * mm, "end": v(46, -19.9) * mm});
            skArc(sketch, "E250", {"start": v(46, -19.9) * mm, "mid": v(44.4, -20.94) * mm, "end": v(42.73, -21.86) * mm});
            skArc(sketch, "E251", {"start": v(42.73, -21.86) * mm, "mid": v(39.08, -23.46) * mm, "end": v(35.27, -24.6) * mm});
            skArc(sketch, "E252", {"start": v(35.27, -24.6) * mm, "mid": v(30.2, -25.64) * mm, "end": v(25.1, -26.4) * mm});
            skArc(sketch, "E253", {"start": v(25.1, -26.4) * mm, "mid": v(20.25, -26.87) * mm, "end": v(15.37, -27.15) * mm});
            skArc(sketch, "E254", {"start": v(15.37, -27.15) * mm, "mid": v(13.6, -26.74) * mm, "end": v(12.24, -25.5) * mm});
            skArc(sketch, "E255", {"start": v(12.24, -25.5) * mm, "mid": v(11.3, -24.62) * mm, "end": v(10.07, -24.27) * mm});
            skArc(sketch, "E256", {"start": v(10.07, -24.27) * mm, "mid": v(4.98, -24.18) * mm, "end": v(-0.1, -24.16) * mm});
            skArc(sketch, "E257", {"start": v(-0.1, -24.16) * mm, "mid": v(-5.16, -24.24) * mm, "end": v(-10.22, -24.4) * mm});
            skArc(sketch, "E258", {"start": v(-10.22, -24.4) * mm, "mid": v(-11.57, -24.76) * mm, "end": v(-12.65, -25.65) * mm});
            skArc(sketch, "E259", {"start": v(-12.65, -25.65) * mm, "mid": v(-13.7, -26.5) * mm, "end": v(-15, -26.8) * mm});
            skArc(sketch, "E260", {"start": v(-15, -26.8) * mm, "mid": v(-18.65, -26.71) * mm, "end": v(-22.29, -26.5) * mm});
            skArc(sketch, "E261", {"start": v(-22.29, -26.5) * mm, "mid": v(-26.3, -26.1) * mm, "end": v(-30.28, -25.5) * mm});
            skArc(sketch, "E262", {"start": v(-30.28, -25.5) * mm, "mid": v(-33.83, -24.77) * mm, "end": v(-37.32, -23.8) * mm});
            skArc(sketch, "E263", {"start": v(-37.32, -23.8) * mm, "mid": v(-40, -22.82) * mm, "end": v(-42.6, -21.62) * mm});
            skArc(sketch, "E264", {"start": v(-42.6, -21.62) * mm, "mid": v(-44.82, -20.32) * mm, "end": v(-46.88, -18.76) * mm});
            skArc(sketch, "E265", {"start": v(-46.88, -18.76) * mm, "mid": v(-48.5, -17.19) * mm, "end": v(-49.88, -15.42) * mm});
            skArc(sketch, "E266", {"start": v(-49.88, -15.42) * mm, "mid": v(-51.3, -12.13) * mm, "end": v(-52.03, -8.62) * mm});
            skLineSegment(sketch, "E267", {"start": v(-52.03, -8.62) * mm, "end": v(-53.04, -9.25) * mm});
            skArc(sketch, "E268", {"start": v(-53.04, -9.25) * mm, "mid": v(-54.15, -10.56) * mm, "end": v(-54.26, -12.28) * mm});
            skArc(sketch, "E269", {"start": v(-54.26, -12.28) * mm, "mid": v(-53.26, -15.4) * mm, "end": v(-51.9, -18.36) * mm});
            skArc(sketch, "E270", {"start": v(-51.9, -18.36) * mm, "mid": v(-49.46, -22.6) * mm, "end": v(-46.69, -26.62) * mm});
            skArc(sketch, "E271", {"start": v(-46.69, -26.62) * mm, "mid": v(-42.7, -31.76) * mm, "end": v(-38.55, -36.75) * mm});
            skArc(sketch, "E272", {"start": v(-38.55, -36.75) * mm, "mid": v(-34.5, -41.53) * mm, "end": v(-30.55, -46.37) * mm});
            skArc(sketch, "E273", {"start": v(-30.55, -46.37) * mm, "mid": v(-27.65, -50.13) * mm, "end": v(-24.9, -54) * mm});
            skArc(sketch, "E274", {"start": v(-24.9, -54) * mm, "mid": v(-22.9, -57.07) * mm, "end": v(-21.06, -60.24) * mm});
            skArc(sketch, "E275", {"start": v(-21.06, -60.24) * mm, "mid": v(-19.08, -64.9) * mm, "end": v(-17.62, -69.75) * mm});
            skLineSegment(sketch, "E276", {"start": v(-17.62, -69.75) * mm, "end": v(-0.05, -69.75) * mm});
            skLineSegment(sketch, "E277", {"start": v(-0.05, -69.75) * mm, "end": v(17.53, -69.75) * mm});
            skLineSegment(sketch, "E278", {"start": v(17.53, -69.75) * mm, "end": v(18.67, -65.5) * mm});
            skArc(sketch, "E279", {"start": v(40.68, -62.5) * mm, "mid": v(42.95, -59.14) * mm, "end": v(45.16, -55.73) * mm});
            skArc(sketch, "E280", {"start": v(45.16, -55.73) * mm, "mid": v(46.36, -53.63) * mm, "end": v(47.38, -51.45) * mm});
            skArc(sketch, "E281", {"start": v(47.38, -51.45) * mm, "mid": v(48.1, -49.45) * mm, "end": v(48.58, -47.38) * mm});
            skArc(sketch, "E282", {"start": v(48.58, -47.38) * mm, "mid": v(49.45, -40.83) * mm, "end": v(50, -34.25) * mm});
            skLineSegment(sketch, "E283", {"start": v(50, -34.25) * mm, "end": v(45.84, -41.25) * mm});
            skArc(sketch, "E284", {"start": v(45.84, -41.25) * mm, "mid": v(43.48, -45.32) * mm, "end": v(41.22, -49.44) * mm});
            skArc(sketch, "E285", {"start": v(41.22, -49.44) * mm, "mid": v(39.44, -52.92) * mm, "end": v(37.8, -56.46) * mm});
            skArc(sketch, "E286", {"start": v(37.8, -56.46) * mm, "mid": v(36.62, -59.3) * mm, "end": v(35.57, -62.18) * mm});
            skArc(sketch, "E287", {"start": v(35.57, -62.18) * mm, "mid": v(34.95, -65.94) * mm, "end": v(34.94, -69.75) * mm});
            skLineSegment(sketch, "E288", {"start": v(34.94, -69.75) * mm, "end": v(35.32, -69.75) * mm});
            skArc(sketch, "E289", {"start": v(35.32, -69.75) * mm, "mid": v(35.45, -69.72) * mm, "end": v(35.55, -69.64) * mm});
            skArc(sketch, "E290", {"start": v(35.55, -69.64) * mm, "mid": v(36.3, -68.63) * mm, "end": v(37.05, -67.62) * mm});
            skArc(sketch, "E291", {"start": v(37.05, -67.62) * mm, "mid": v(37.9, -66.46) * mm, "end": v(38.74, -65.28) * mm});
            skArc(sketch, "E292", {"start": v(38.74, -65.28) * mm, "mid": v(39.72, -63.9) * mm, "end": v(40.68, -62.5) * mm});
            skLineSegment(sketch, "E293", {"start": v(-16.06, -21.5) * mm, "end": v(-16.06, -20.25) * mm});
            skLineSegment(sketch, "E294", {"start": v(-16.06, -20.25) * mm, "end": v(-0.06, -20.25) * mm});
            skLineSegment(sketch, "E295", {"start": v(-0.06, -20.25) * mm, "end": v(15.94, -20.25) * mm});
            skLineSegment(sketch, "E296", {"start": v(15.94, -20.25) * mm, "end": v(15.94, -21.65) * mm});
            skLineSegment(sketch, "E297", {"start": v(15.94, -21.65) * mm, "end": v(15.94, -23.05) * mm});
            skLineSegment(sketch, "E298", {"start": v(15.94, -23.05) * mm, "end": v(23.83, -22.44) * mm});
            skArc(sketch, "E299", {"start": v(23.83, -22.44) * mm, "mid": v(29.21, -21.79) * mm, "end": v(34.53, -20.67) * mm});
            skArc(sketch, "E300", {"start": v(34.53, -20.67) * mm, "mid": v(38.65, -19.23) * mm, "end": v(42.49, -17.13) * mm});
            skArc(sketch, "E301", {"start": v(42.49, -17.13) * mm, "mid": v(44.74, -15.14) * mm, "end": v(46.34, -12.59) * mm});
            skArc(sketch, "E302", {"start": v(46.34, -12.59) * mm, "mid": v(46.5, -9.32) * mm, "end": v(45.08, -6.36) * mm});
            skLineSegment(sketch, "E303", {"start": v(45.08, -6.36) * mm, "end": v(36.26, -10.52) * mm});
            skArc(sketch, "E304", {"start": v(36.26, -10.52) * mm, "mid": v(32.06, -12.42) * mm, "end": v(27.79, -14.16) * mm});
            skArc(sketch, "E305", {"start": v(27.79, -14.16) * mm, "mid": v(24.22, -15.4) * mm, "end": v(20.58, -16.43) * mm});
            skArc(sketch, "E306", {"start": v(20.58, -16.43) * mm, "mid": v(16.85, -17.21) * mm, "end": v(13.08, -17.76) * mm});
            skArc(sketch, "E307", {"start": v(13.08, -17.76) * mm, "mid": v(8.38, -18.2) * mm, "end": v(3.66, -18.49) * mm});
            skArc(sketch, "E308", {"start": v(3.66, -18.49) * mm, "mid": v(-2.1, -18.6) * mm, "end": v(-7.86, -18.43) * mm});
            skArc(sketch, "E309", {"start": v(-7.86, -18.43) * mm, "mid": v(-12.86, -17.97) * mm, "end": v(-17.8, -17.15) * mm});
            skArc(sketch, "E310", {"start": v(-17.8, -17.15) * mm, "mid": v(-22.6, -15.98) * mm, "end": v(-27.3, -14.45) * mm});
            skArc(sketch, "E311", {"start": v(-27.3, -14.45) * mm, "mid": v(-32.44, -12.4) * mm, "end": v(-37.46, -10.08) * mm});
            skArc(sketch, "E312", {"start": v(-37.46, -10.08) * mm, "mid": v(-38.82, -9.42) * mm, "end": v(-40.2, -8.8) * mm});
            skArc(sketch, "E313", {"start": v(-40.2, -8.8) * mm, "mid": v(-41.46, -8.29) * mm, "end": v(-42.73, -7.81) * mm});
            skArc(sketch, "E314", {"start": v(-42.73, -7.81) * mm, "mid": v(-43.78, -7.46) * mm, "end": v(-44.84, -7.14) * mm});
            skArc(sketch, "E315", {"start": v(-44.84, -7.14) * mm, "mid": v(-46, -7.23) * mm, "end": v(-47.06, -7.7) * mm});
            skLineSegment(sketch, "E316", {"start": v(-47.06, -7.7) * mm, "end": v(-47.06, -9.79) * mm});
            skArc(sketch, "E317", {"start": v(-47.06, -9.79) * mm, "mid": v(-47.04, -10.26) * mm, "end": v(-46.98, -10.73) * mm});
            skArc(sketch, "E318", {"start": v(-46.98, -10.73) * mm, "mid": v(-46.88, -11.29) * mm, "end": v(-46.75, -11.84) * mm});
            skArc(sketch, "E319", {"start": v(-46.75, -11.84) * mm, "mid": v(-46.6, -12.38) * mm, "end": v(-46.42, -12.92) * mm});
            skArc(sketch, "E320", {"start": v(-46.42, -12.92) * mm, "mid": v(-46.24, -13.38) * mm, "end": v(-46.02, -13.82) * mm});
            skArc(sketch, "E321", {"start": v(-46.02, -13.82) * mm, "mid": v(-44.73, -15.54) * mm, "end": v(-43, -16.8) * mm});
            skArc(sketch, "E322", {"start": v(-43, -16.8) * mm, "mid": v(-39.69, -18.36) * mm, "end": v(-36.28, -19.69) * mm});
            skArc(sketch, "E323", {"start": v(-36.28, -19.69) * mm, "mid": v(-32.35, -20.91) * mm, "end": v(-28.35, -21.86) * mm});
            skArc(sketch, "E324", {"start": v(-28.35, -21.86) * mm, "mid": v(-22.22, -22.58) * mm, "end": v(-16.06, -22.75) * mm});
            skLineSegment(sketch, "E325", {"start": v(-16.06, -22.75) * mm, "end": v(-16.06, -21.5) * mm});
            skArc(sketch, "E326", {"start": v(22.44, -11.75) * mm, "mid": v(25.48, -10.72) * mm, "end": v(28.46, -9.56) * mm});
            skArc(sketch, "E327", {"start": v(28.46, -9.56) * mm, "mid": v(31.93, -8.08) * mm, "end": v(35.35, -6.5) * mm});
            skArc(sketch, "E328", {"start": v(35.35, -6.5) * mm, "mid": v(38.55, -4.95) * mm, "end": v(41.74, -3.35) * mm});
            skArc(sketch, "E329", {"start": v(41.74, -3.35) * mm, "mid": v(42.68, -2.7) * mm, "end": v(43.4, -1.81) * mm});
            skArc(sketch, "E330", {"start": v(43.4, -1.81) * mm, "mid": v(43.6, -1.4) * mm, "end": v(43.7, -0.97) * mm});
            skArc(sketch, "E331", {"start": v(43.7, -0.97) * mm, "mid": v(44.2, 3.4) * mm, "end": v(44.68, 7.79) * mm});
            skArc(sketch, "E332", {"start": v(44.68, 7.79) * mm, "mid": v(45.23, 12.78) * mm, "end": v(45.74, 17.78) * mm});
            skArc(sketch, "E333", {"start": v(45.74, 17.78) * mm, "mid": v(46.32, 23.62) * mm, "end": v(46.88, 29.46) * mm});
            skArc(sketch, "E334", {"start": v(46.88, 29.46) * mm, "mid": v(47.82, 39.5) * mm, "end": v(48.74, 49.54) * mm});
            skArc(sketch, "E335", {"start": v(48.74, 49.54) * mm, "mid": v(49, 52.94) * mm, "end": v(49.14, 56.35) * mm});
            skArc(sketch, "E336", {"start": v(49.14, 56.35) * mm, "mid": v(49.1, 58.24) * mm, "end": v(48.86, 60.1) * mm});
            skArc(sketch, "E337", {"start": v(48.86, 60.1) * mm, "mid": v(48.46, 61.58) * mm, "end": v(47.79, 62.96) * mm});
            skArc(sketch, "E338", {"start": v(47.79, 62.96) * mm, "mid": v(46.06, 65.37) * mm, "end": v(43.99, 67.5) * mm});
            skArc(sketch, "E339", {"start": v(43.99, 67.5) * mm, "mid": v(41.22, 69.75) * mm, "end": v(38.26, 71.75) * mm});
            skArc(sketch, "E340", {"start": v(38.26, 71.75) * mm, "mid": v(35.13, 73.5) * mm, "end": v(31.86, 74.99) * mm});
            skArc(sketch, "E341", {"start": v(31.86, 74.99) * mm, "mid": v(27.27, 76.2) * mm, "end": v(22.56, 76.75) * mm});
            skLineSegment(sketch, "E342", {"start": v(22.56, 76.75) * mm, "end": v(19.38, 50.39) * mm});
            skArc(sketch, "E343", {"start": v(19.38, 50.39) * mm, "mid": v(18.63, 44.27) * mm, "end": v(17.84, 38.15) * mm});
            skArc(sketch, "E344", {"start": v(17.84, 38.15) * mm, "mid": v(17.27, 34.1) * mm, "end": v(16.63, 30.05) * mm});
            skArc(sketch, "E345", {"start": v(16.63, 30.05) * mm, "mid": v(16.13, 27.16) * mm, "end": v(15.6, 24.28) * mm});
            skArc(sketch, "E346", {"start": v(15.6, 24.28) * mm, "mid": v(15.33, 23.64) * mm, "end": v(14.83, 23.15) * mm});
            skArc(sketch, "E347", {"start": v(14.83, 23.15) * mm, "mid": v(13.3, 22.46) * mm, "end": v(11.66, 22.22) * mm});
            skArc(sketch, "E348", {"start": v(11.66, 22.22) * mm, "mid": v(5.36, 22.2) * mm, "end": v(-0.95, 22.23) * mm});
            skArc(sketch, "E349", {"start": v(-0.95, 22.23) * mm, "mid": v(-7.44, 22.33) * mm, "end": v(-13.92, 22.47) * mm});
            skArc(sketch, "E350", {"start": v(-13.92, 22.47) * mm, "mid": v(-14.95, 22.76) * mm, "end": v(-15.72, 23.5) * mm});
            skArc(sketch, "E351", {"start": v(-15.72, 23.5) * mm, "mid": v(-15.96, 24) * mm, "end": v(-16.1, 24.52) * mm});
            skArc(sketch, "E352", {"start": v(-16.1, 24.52) * mm, "mid": v(-16.65, 28.24) * mm, "end": v(-17.2, 31.95) * mm});
            skArc(sketch, "E353", {"start": v(-17.2, 31.95) * mm, "mid": v(-17.8, 36.25) * mm, "end": v(-18.38, 40.56) * mm});
            skArc(sketch, "E354", {"start": v(-18.38, 40.56) * mm, "mid": v(-19.02, 45.54) * mm, "end": v(-19.64, 50.53) * mm});
            skArc(sketch, "E355", {"start": v(-19.64, 50.53) * mm, "mid": v(-20.26, 55.49) * mm, "end": v(-20.88, 60.45) * mm});
            skArc(sketch, "E356", {"start": v(-20.88, 60.45) * mm, "mid": v(-21.43, 64.66) * mm, "end": v(-22, 68.87) * mm});
            skArc(sketch, "E357", {"start": v(-22, 68.87) * mm, "mid": v(-22.51, 72.6) * mm, "end": v(-23.03, 76.33) * mm});
            skArc(sketch, "E358", {"start": v(-23.03, 76.33) * mm, "mid": v(-23.1, 76.57) * mm, "end": v(-23.25, 76.77) * mm});
            skArc(sketch, "E359", {"start": v(-23.25, 76.77) * mm, "mid": v(-23.86, 77.12) * mm, "end": v(-24.57, 77.12) * mm});
            skArc(sketch, "E360", {"start": v(-24.57, 77.12) * mm, "mid": v(-27.01, 76.43) * mm, "end": v(-29.44, 75.68) * mm});
            skArc(sketch, "E361", {"start": v(-29.44, 75.68) * mm, "mid": v(-31.96, 74.81) * mm, "end": v(-34.44, 73.85) * mm});
            skArc(sketch, "E362", {"start": v(-34.44, 73.85) * mm, "mid": v(-36.42, 72.96) * mm, "end": v(-38.34, 71.93) * mm});
            skArc(sketch, "E363", {"start": v(-38.34, 71.93) * mm, "mid": v(-39.36, 71.29) * mm, "end": v(-40.35, 70.59) * mm});
            skArc(sketch, "E364", {"start": v(-40.35, 70.59) * mm, "mid": v(-41.5, 69.7) * mm, "end": v(-42.62, 68.76) * mm});
            skArc(sketch, "E365", {"start": v(-42.62, 68.76) * mm, "mid": v(-43.71, 67.79) * mm, "end": v(-44.78, 66.77) * mm});
            skArc(sketch, "E366", {"start": v(-44.78, 66.77) * mm, "mid": v(-45.64, 65.87) * mm, "end": v(-46.46, 64.93) * mm});
            skArc(sketch, "E367", {"start": v(-46.46, 64.93) * mm, "mid": v(-47.6, 63.25) * mm, "end": v(-48.45, 61.39) * mm});
            skArc(sketch, "E368", {"start": v(-48.45, 61.39) * mm, "mid": v(-48.98, 59.35) * mm, "end": v(-49.19, 57.25) * mm});
            skArc(sketch, "E369", {"start": v(-49.19, 57.25) * mm, "mid": v(-49.16, 53.67) * mm, "end": v(-48.95, 50.09) * mm});
            skArc(sketch, "E370", {"start": v(-48.95, 50.09) * mm, "mid": v(-48.05, 39.72) * mm, "end": v(-47.11, 29.36) * mm});
            skArc(sketch, "E371", {"start": v(-47.11, 29.36) * mm, "mid": v(-46.56, 23.36) * mm, "end": v(-45.99, 17.36) * mm});
            skArc(sketch, "E372", {"start": v(-45.99, 17.36) * mm, "mid": v(-45.5, 12.28) * mm, "end": v(-44.98, 7.2) * mm});
            skArc(sketch, "E373", {"start": v(-44.98, 7.2) * mm, "mid": v(-44.52, 2.66) * mm, "end": v(-44.05, -1.88) * mm});
            skArc(sketch, "E374", {"start": v(-44.05, -1.88) * mm, "mid": v(-44, -2.03) * mm, "end": v(-43.9, -2.15) * mm});
            skArc(sketch, "E375", {"start": v(-43.9, -2.15) * mm, "mid": v(-41.48, -3.75) * mm, "end": v(-38.94, -5.14) * mm});
            skArc(sketch, "E376", {"start": v(-38.94, -5.14) * mm, "mid": v(-35.37, -6.82) * mm, "end": v(-31.75, -8.37) * mm});
            skArc(sketch, "E377", {"start": v(-31.75, -8.37) * mm, "mid": v(-27.83, -9.9) * mm, "end": v(-23.86, -11.29) * mm});
            skArc(sketch, "E378", {"start": v(-23.86, -11.29) * mm, "mid": v(-20.23, -12.4) * mm, "end": v(-16.56, -13.33) * mm});
            skArc(sketch, "E379", {"start": v(-16.56, -13.33) * mm, "mid": v(-12.46, -14.08) * mm, "end": v(-8.31, -14.43) * mm});
            skArc(sketch, "E380", {"start": v(-8.31, -14.43) * mm, "mid": v(-2.64, -14.53) * mm, "end": v(3.03, -14.4) * mm});
            skArc(sketch, "E381", {"start": v(3.03, -14.4) * mm, "mid": v(8.69, -14.07) * mm, "end": v(14.33, -13.51) * mm});
            skArc(sketch, "E382", {"start": v(14.33, -13.51) * mm, "mid": v(18.43, -12.83) * mm, "end": v(22.44, -11.75) * mm});
            skArc(sketch, "E383", {"start": v(-54.14, 33.11) * mm, "mid": v(-54.1, 42.5) * mm, "end": v(-54.02, 51.87) * mm});
            skArc(sketch, "E384", {"start": v(-54.02, 51.87) * mm, "mid": v(-53.9, 55.21) * mm, "end": v(-53.62, 58.54) * mm});
            skArc(sketch, "E385", {"start": v(-53.62, 58.54) * mm, "mid": v(-53.24, 60.6) * mm, "end": v(-52.59, 62.58) * mm});
            skArc(sketch, "E386", {"start": v(-52.59, 62.58) * mm, "mid": v(-51.64, 64.55) * mm, "end": v(-50.46, 66.38) * mm});
            skArc(sketch, "E387", {"start": v(-50.46, 66.38) * mm, "mid": v(-49.71, 67.37) * mm, "end": v(-48.94, 68.33) * mm});
            skArc(sketch, "E388", {"start": v(-48.94, 68.33) * mm, "mid": v(-48.16, 69.25) * mm, "end": v(-47.36, 70.14) * mm});
            skArc(sketch, "E389", {"start": v(-47.36, 70.14) * mm, "mid": v(-46.65, 70.88) * mm, "end": v(-45.92, 71.6) * mm});
            skArc(sketch, "E390", {"start": v(-45.92, 71.6) * mm, "mid": v(-45.46, 71.98) * mm, "end": v(-44.96, 72.3) * mm});
            skArc(sketch, "E391", {"start": v(-44.96, 72.3) * mm, "mid": v(-44.48, 72.62) * mm, "end": v(-44.06, 73.02) * mm});
            skArc(sketch, "E392", {"start": v(-44.06, 73.02) * mm, "mid": v(-43.73, 73.5) * mm, "end": v(-43.48, 74.02) * mm});
            skArc(sketch, "E393", {"start": v(-43.48, 74.02) * mm, "mid": v(-43.28, 74.73) * mm, "end": v(-43.17, 75.45) * mm});
            skArc(sketch, "E394", {"start": v(-43.17, 75.45) * mm, "mid": v(-43.08, 78.6) * mm, "end": v(-43.14, 81.75) * mm});
            skLineSegment(sketch, "E395", {"start": v(-43.14, 81.75) * mm, "end": v(-47.5, 77) * mm});
            skArc(sketch, "E396", {"start": v(-47.5, 77) * mm, "mid": v(-48.44, 75.95) * mm, "end": v(-49.33, 74.87) * mm});
            skArc(sketch, "E397", {"start": v(-49.33, 74.87) * mm, "mid": v(-50.28, 73.65) * mm, "end": v(-51.2, 72.4) * mm});
            skArc(sketch, "E398", {"start": v(-51.2, 72.4) * mm, "mid": v(-52.03, 71.2) * mm, "end": v(-52.84, 69.97) * mm});
            skArc(sketch, "E399", {"start": v(-52.84, 69.97) * mm, "mid": v(-53.41, 69) * mm, "end": v(-53.93, 68) * mm});
            skArc(sketch, "E400", {"start": v(-53.93, 68) * mm, "mid": v(-54.9, 65.7) * mm, "end": v(-55.62, 63.32) * mm});
            skArc(sketch, "E401", {"start": v(-55.62, 63.32) * mm, "mid": v(-56.35, 59.99) * mm, "end": v(-56.95, 56.63) * mm});
            skArc(sketch, "E402", {"start": v(-56.95, 56.63) * mm, "mid": v(-57.48, 52.76) * mm, "end": v(-57.85, 48.87) * mm});
            skArc(sketch, "E403", {"start": v(-57.85, 48.87) * mm, "mid": v(-58.09, 44.81) * mm, "end": v(-58.18, 40.75) * mm});
            skArc(sketch, "E404", {"start": v(-58.18, 40.75) * mm, "mid": v(-58.2, 38.64) * mm, "end": v(-58.23, 36.53) * mm});
            skArc(sketch, "E405", {"start": v(-58.23, 36.53) * mm, "mid": v(-58.3, 33.26) * mm, "end": v(-58.36, 29.99) * mm});
            skArc(sketch, "E406", {"start": v(-58.36, 29.99) * mm, "mid": v(-58.45, 26.3) * mm, "end": v(-58.54, 22.6) * mm});
            skArc(sketch, "E407", {"start": v(-58.54, 22.6) * mm, "mid": v(-58.63, 18.98) * mm, "end": v(-58.73, 15.36) * mm});
            skArc(sketch, "E408", {"start": v(-58.73, 15.36) * mm, "mid": v(-58.81, 11.9) * mm, "end": v(-58.87, 8.44) * mm});
            skArc(sketch, "E409", {"start": v(-58.87, 8.44) * mm, "mid": v(-58.88, 5.23) * mm, "end": v(-58.86, 2.02) * mm});
            skArc(sketch, "E410", {"start": v(-58.86, 2.02) * mm, "mid": v(-58.82, -0.66) * mm, "end": v(-58.75, -3.35) * mm});
            skArc(sketch, "E411", {"start": v(-58.75, -3.35) * mm, "mid": v(-58.37, -6.32) * mm, "end": v(-57.73, -9.25) * mm});
            skLineSegment(sketch, "E412", {"start": v(-57.73, -9.25) * mm, "end": v(-55.97, -2.25) * mm});
            skArc(sketch, "E413", {"start": v(-55.97, -2.25) * mm, "mid": v(-55.44, 0.2) * mm, "end": v(-55.06, 2.67) * mm});
            skArc(sketch, "E414", {"start": v(-55.06, 2.67) * mm, "mid": v(-54.75, 5.72) * mm, "end": v(-54.54, 8.78) * mm});
            skArc(sketch, "E415", {"start": v(-54.54, 8.78) * mm, "mid": v(-54.35, 13.27) * mm, "end": v(-54.25, 17.75) * mm});
            skArc(sketch, "E416", {"start": v(-54.25, 17.75) * mm, "mid": v(-54.18, 25.43) * mm, "end": v(-54.14, 33.11) * mm});
            skArc(sketch, "E417", {"start": v(58.55, 13.75) * mm, "mid": v(58.44, 17.47) * mm, "end": v(58.34, 21.19) * mm});
            skArc(sketch, "E418", {"start": v(58.34, 21.19) * mm, "mid": v(58.25, 24.92) * mm, "end": v(58.18, 28.66) * mm});
            skArc(sketch, "E419", {"start": v(58.18, 28.66) * mm, "mid": v(58.11, 31.93) * mm, "end": v(58.06, 35.2) * mm});
            skArc(sketch, "E420", {"start": v(58.06, 35.2) * mm, "mid": v(58.04, 37.23) * mm, "end": v(58.04, 39.25) * mm});
            skArc(sketch, "E421", {"start": v(58.04, 39.25) * mm, "mid": v(57.98, 43.4) * mm, "end": v(57.76, 47.57) * mm});
            skArc(sketch, "E422", {"start": v(57.76, 47.57) * mm, "mid": v(57.39, 51.74) * mm, "end": v(56.86, 55.9) * mm});
            skArc(sketch, "E423", {"start": v(56.86, 55.9) * mm, "mid": v(56.26, 59.55) * mm, "end": v(55.52, 63.17) * mm});
            skArc(sketch, "E424", {"start": v(55.52, 63.17) * mm, "mid": v(54.82, 65.6) * mm, "end": v(53.86, 67.92) * mm});
            skArc(sketch, "E425", {"start": v(53.86, 67.92) * mm, "mid": v(53.33, 68.94) * mm, "end": v(52.75, 69.92) * mm});
            skArc(sketch, "E426", {"start": v(52.75, 69.92) * mm, "mid": v(51.94, 71.16) * mm, "end": v(51.1, 72.37) * mm});
            skArc(sketch, "E427", {"start": v(51.1, 72.37) * mm, "mid": v(50.17, 73.63) * mm, "end": v(49.22, 74.87) * mm});
            skArc(sketch, "E428", {"start": v(49.22, 74.87) * mm, "mid": v(46.18, 78.36) * mm, "end": v(43.02, 81.75) * mm});
            skLineSegment(sketch, "E429", {"start": v(43.02, 81.75) * mm, "end": v(42.98, 77.88) * mm});
            skArc(sketch, "E430", {"start": v(42.98, 77.88) * mm, "mid": v(43.03, 76.72) * mm, "end": v(43.2, 75.58) * mm});
            skArc(sketch, "E431", {"start": v(43.2, 75.58) * mm, "mid": v(43.5, 74.58) * mm, "end": v(43.93, 73.65) * mm});
            skArc(sketch, "E432", {"start": v(43.93, 73.65) * mm, "mid": v(44.63, 72.52) * mm, "end": v(45.44, 71.47) * mm});
            skArc(sketch, "E433", {"start": v(45.44, 71.47) * mm, "mid": v(46.92, 69.75) * mm, "end": v(48.44, 68.07) * mm});
            skArc(sketch, "E434", {"start": v(48.44, 68.07) * mm, "mid": v(50.2, 65.96) * mm, "end": v(51.7, 63.66) * mm});
            skArc(sketch, "E435", {"start": v(51.7, 63.66) * mm, "mid": v(52.68, 61.57) * mm, "end": v(53.26, 59.33) * mm});
            skArc(sketch, "E436", {"start": v(53.26, 59.33) * mm, "mid": v(53.67, 55.93) * mm, "end": v(53.84, 52.5) * mm});
            skArc(sketch, "E437", {"start": v(53.84, 52.5) * mm, "mid": v(53.92, 43.15) * mm, "end": v(53.94, 33.81) * mm});
            skArc(sketch, "E438", {"start": v(53.94, 33.81) * mm, "mid": v(53.96, 26.36) * mm, "end": v(54.01, 18.91) * mm});
            skArc(sketch, "E439", {"start": v(54.01, 18.91) * mm, "mid": v(54.1, 14.3) * mm, "end": v(54.27, 9.67) * mm});
            skArc(sketch, "E440", {"start": v(54.27, 9.67) * mm, "mid": v(54.47, 6.44) * mm, "end": v(54.76, 3.22) * mm});
            skArc(sketch, "E441", {"start": v(54.76, 3.22) * mm, "mid": v(55.83, -3) * mm, "end": v(57.25, -9.15) * mm});
            skLineSegment(sketch, "E442", {"start": v(57.25, -9.15) * mm, "end": v(58.17, -6.7) * mm});
            skArc(sketch, "E443", {"start": v(58.17, -6.7) * mm, "mid": v(58.4, -5.86) * mm, "end": v(58.5, -5) * mm});
            skArc(sketch, "E444", {"start": v(58.5, -5) * mm, "mid": v(58.6, -2.35) * mm, "end": v(58.66, 0.3) * mm});
            skArc(sketch, "E445", {"start": v(58.66, 0.3) * mm, "mid": v(58.7, 3.47) * mm, "end": v(58.69, 6.65) * mm});
            skArc(sketch, "E446", {"start": v(58.69, 6.65) * mm, "mid": v(58.63, 10.2) * mm, "end": v(58.55, 13.75) * mm});
            skLineSegment(sketch, "E447", {"start": v(-48.9, 4.8) * mm, "end": v(-49.63, 11.75) * mm});
            skLineSegment(sketch, "E448", {"start": v(-49.63, 11.75) * mm, "end": v(-50.36, 5.12) * mm});
            skArc(sketch, "E449", {"start": v(-50.36, 5.12) * mm, "mid": v(-50.49, 3.79) * mm, "end": v(-50.59, 2.45) * mm});
            skArc(sketch, "E450", {"start": v(-50.59, 2.45) * mm, "mid": v(-50.65, 1.2) * mm, "end": v(-50.68, -0.07) * mm});
            skArc(sketch, "E451", {"start": v(-50.68, -0.07) * mm, "mid": v(-50.67, -1.13) * mm, "end": v(-50.64, -2.2) * mm});
            skArc(sketch, "E452", {"start": v(-50.64, -2.2) * mm, "mid": v(-50.31, -3.62) * mm, "end": v(-49.76, -4.97) * mm});
            skLineSegment(sketch, "E453", {"start": v(-49.76, -4.97) * mm, "end": v(-48.97, -3.56) * mm});
            skArc(sketch, "E454", {"start": v(-48.97, -3.56) * mm, "mid": v(-48.78, -3.12) * mm, "end": v(-48.7, -2.65) * mm});
            skArc(sketch, "E455", {"start": v(-48.7, -2.65) * mm, "mid": v(-48.65, -1.59) * mm, "end": v(-48.63, -0.53) * mm});
            skArc(sketch, "E456", {"start": v(-48.63, -0.53) * mm, "mid": v(-48.64, 0.75) * mm, "end": v(-48.69, 2.03) * mm});
            skArc(sketch, "E457", {"start": v(-48.69, 2.03) * mm, "mid": v(-48.78, 3.41) * mm, "end": v(-48.9, 4.8) * mm});
            skLineSegment(sketch, "E458", {"start": v(50.13, 5.85) * mm, "end": v(49.38, 13.75) * mm});
            skLineSegment(sketch, "E459", {"start": v(49.38, 13.75) * mm, "end": v(48.68, 5.37) * mm});
            skArc(sketch, "E460", {"start": v(48.68, 5.37) * mm, "mid": v(48.56, 3.73) * mm, "end": v(48.46, 2.08) * mm});
            skArc(sketch, "E461", {"start": v(48.46, 2.08) * mm, "mid": v(48.4, 0.62) * mm, "end": v(48.37, -0.85) * mm});
            skArc(sketch, "E462", {"start": v(48.37, -0.85) * mm, "mid": v(48.37, -2.06) * mm, "end": v(48.39, -3.28) * mm});
            skArc(sketch, "E463", {"start": v(48.39, -3.28) * mm, "mid": v(48.69, -4.2) * mm, "end": v(49.22, -5.01) * mm});
            skLineSegment(sketch, "E464", {"start": v(49.22, -5.01) * mm, "end": v(50.05, -3.53) * mm});
            skArc(sketch, "E465", {"start": v(50.05, -3.53) * mm, "mid": v(50.25, -3.06) * mm, "end": v(50.33, -2.55) * mm});
            skArc(sketch, "E466", {"start": v(50.33, -2.55) * mm, "mid": v(50.39, -1.36) * mm, "end": v(50.41, -0.17) * mm});
            skArc(sketch, "E467", {"start": v(50.41, -0.17) * mm, "mid": v(50.4, 1.27) * mm, "end": v(50.35, 2.71) * mm});
            skArc(sketch, "E468", {"start": v(50.35, 2.71) * mm, "mid": v(50.26, 4.28) * mm, "end": v(50.13, 5.85) * mm});
            skArc(sketch, "E469", {"start": v(14.6, 44) * mm, "mid": v(14.98, 47.36) * mm, "end": v(15.33, 50.72) * mm});
            skArc(sketch, "E470", {"start": v(15.33, 50.72) * mm, "mid": v(15.58, 53.5) * mm, "end": v(15.78, 56.3) * mm});
            skArc(sketch, "E471", {"start": v(15.78, 56.3) * mm, "mid": v(15.92, 58.57) * mm, "end": v(16.03, 60.86) * mm});
            skArc(sketch, "E472", {"start": v(16.03, 60.86) * mm, "mid": v(15.96, 61.33) * mm, "end": v(15.72, 61.75) * mm});
            skArc(sketch, "E473", {"start": v(15.72, 61.75) * mm, "mid": v(15.35, 62.04) * mm, "end": v(14.9, 62.17) * mm});
            skArc(sketch, "E474", {"start": v(14.9, 62.17) * mm, "mid": v(12.9, 62.33) * mm, "end": v(10.9, 62.46) * mm});
            skArc(sketch, "E475", {"start": v(10.9, 62.46) * mm, "mid": v(8.42, 62.6) * mm, "end": v(5.95, 62.68) * mm});
            skArc(sketch, "E476", {"start": v(5.95, 62.68) * mm, "mid": v(2.95, 62.73) * mm, "end": v(-0.06, 62.75) * mm});
            skArc(sketch, "E477", {"start": v(-0.06, 62.75) * mm, "mid": v(-3.05, 62.73) * mm, "end": v(-6.05, 62.68) * mm});
            skArc(sketch, "E478", {"start": v(-6.05, 62.68) * mm, "mid": v(-8.53, 62.6) * mm, "end": v(-11.01, 62.46) * mm});
            skArc(sketch, "E479", {"start": v(-11.01, 62.46) * mm, "mid": v(-13.02, 62.33) * mm, "end": v(-15.03, 62.16) * mm});
            skArc(sketch, "E480", {"start": v(-15.03, 62.16) * mm, "mid": v(-15.5, 62.03) * mm, "end": v(-15.9, 61.75) * mm});
            skArc(sketch, "E481", {"start": v(-15.9, 61.75) * mm, "mid": v(-16.16, 61.3) * mm, "end": v(-16.25, 60.8) * mm});
            skArc(sketch, "E482", {"start": v(-16.25, 60.8) * mm, "mid": v(-16.16, 58.67) * mm, "end": v(-16.04, 56.55) * mm});
            skArc(sketch, "E483", {"start": v(-16.04, 56.55) * mm, "mid": v(-15.84, 53.82) * mm, "end": v(-15.59, 51.1) * mm});
            skArc(sketch, "E484", {"start": v(-15.59, 51.1) * mm, "mid": v(-14.23, 39.16) * mm, "end": v(-12.76, 27.25) * mm});
            skLineSegment(sketch, "E485", {"start": v(-12.76, 27.25) * mm, "end": v(-0.09, 27.25) * mm});
            skLineSegment(sketch, "E486", {"start": v(-0.09, 27.25) * mm, "end": v(12.6, 27.25) * mm});
            skLineSegment(sketch, "E487", {"start": v(12.6, 27.25) * mm, "end": v(14.6, 44) * mm});
            skArc(sketch, "E488", {"start": v(17.52, 68.75) * mm, "mid": v(17.65, 69.37) * mm, "end": v(17.75, 70) * mm});
            skArc(sketch, "E489", {"start": v(17.75, 70) * mm, "mid": v(17.92, 71.48) * mm, "end": v(18.08, 72.95) * mm});
            skArc(sketch, "E490", {"start": v(18.08, 72.95) * mm, "mid": v(18.25, 74.7) * mm, "end": v(18.42, 76.46) * mm});
            skArc(sketch, "E491", {"start": v(18.42, 76.46) * mm, "mid": v(18.95, 83.1) * mm, "end": v(19.44, 89.75) * mm});
            skLineSegment(sketch, "E492", {"start": v(19.44, 89.75) * mm, "end": v(20.94, 89.75) * mm});
            skLineSegment(sketch, "E493", {"start": v(20.94, 89.75) * mm, "end": v(22.44, 89.75) * mm});
            skLineSegment(sketch, "E494", {"start": v(22.44, 89.75) * mm, "end": v(22.75, 85.5) * mm});
            skLineSegment(sketch, "E495", {"start": v(22.75, 85.5) * mm, "end": v(23.06, 81.26) * mm});
            skLineSegment(sketch, "E496", {"start": v(23.06, 81.26) * mm, "end": v(25.75, 80.68) * mm});
            skArc(sketch, "E497", {"start": v(25.75, 80.68) * mm, "mid": v(26.43, 80.53) * mm, "end": v(27.1, 80.36) * mm});
            skArc(sketch, "E498", {"start": v(27.1, 80.36) * mm, "mid": v(28.07, 80.11) * mm, "end": v(29.03, 79.85) * mm});
            skArc(sketch, "E499", {"start": v(29.03, 79.85) * mm, "mid": v(30.09, 79.56) * mm, "end": v(31.14, 79.26) * mm});
            skArc(sketch, "E500", {"start": v(31.14, 79.26) * mm, "mid": v(32.14, 78.97) * mm, "end": v(33.13, 78.68) * mm});
            skArc(sketch, "E501", {"start": v(33.13, 78.68) * mm, "mid": v(34.05, 78.4) * mm, "end": v(34.97, 78.13) * mm});
            skArc(sketch, "E502", {"start": v(34.97, 78.13) * mm, "mid": v(35.79, 77.9) * mm, "end": v(36.6, 77.67) * mm});
            skArc(sketch, "E503", {"start": v(36.6, 77.67) * mm, "mid": v(37.3, 77.48) * mm, "end": v(38, 77.3) * mm});
            skArc(sketch, "E504", {"start": v(38, 77.3) * mm, "mid": v(38.47, 77.24) * mm, "end": v(38.94, 77.25) * mm});
            skLineSegment(sketch, "E505", {"start": v(38.94, 77.25) * mm, "end": v(38.94, 80.6) * mm});
            skArc(sketch, "E506", {"start": v(38.94, 80.6) * mm, "mid": v(38.66, 82.45) * mm, "end": v(37.84, 84.15) * mm});
            skArc(sketch, "E507", {"start": v(37.84, 84.15) * mm, "mid": v(36.43, 85.84) * mm, "end": v(34.72, 87.24) * mm});
            skArc(sketch, "E508", {"start": v(34.72, 87.24) * mm, "mid": v(31.99, 88.87) * mm, "end": v(29.09, 90.18) * mm});
            skArc(sketch, "E509", {"start": v(29.09, 90.18) * mm, "mid": v(24.54, 91.86) * mm, "end": v(19.93, 93.38) * mm});
            skArc(sketch, "E510", {"start": v(19.93, 93.38) * mm, "mid": v(17.73, 94.02) * mm, "end": v(15.5, 94.58) * mm});
            skArc(sketch, "E511", {"start": v(15.5, 94.58) * mm, "mid": v(13.5, 94.98) * mm, "end": v(11.49, 95.27) * mm});
            skArc(sketch, "E512", {"start": v(11.49, 95.27) * mm, "mid": v(9.14, 95.5) * mm, "end": v(6.78, 95.62) * mm});
            skArc(sketch, "E513", {"start": v(6.78, 95.62) * mm, "mid": v(3.36, 95.7) * mm, "end": v(-0.06, 95.72) * mm});
            skArc(sketch, "E514", {"start": v(-0.06, 95.72) * mm, "mid": v(-4.9, 95.61) * mm, "end": v(-9.75, 95.3) * mm});
            skArc(sketch, "E515", {"start": v(-9.75, 95.3) * mm, "mid": v(-13.82, 94.8) * mm, "end": v(-17.85, 94.02) * mm});
            skArc(sketch, "E516", {"start": v(-17.85, 94.02) * mm, "mid": v(-21.66, 92.98) * mm, "end": v(-25.39, 91.67) * mm});
            skArc(sketch, "E517", {"start": v(-25.39, 91.67) * mm, "mid": v(-29.4, 89.95) * mm, "end": v(-33.3, 88.02) * mm});
            skArc(sketch, "E518", {"start": v(-33.3, 88.02) * mm, "mid": v(-35.08, 87.05) * mm, "end": v(-36.82, 86.05) * mm});
            skArc(sketch, "E519", {"start": v(-36.82, 86.05) * mm, "mid": v(-37.58, 85.51) * mm, "end": v(-38.24, 84.85) * mm});
            skArc(sketch, "E520", {"start": v(-38.24, 84.85) * mm, "mid": v(-38.65, 84.2) * mm, "end": v(-38.87, 83.46) * mm});
            skArc(sketch, "E521", {"start": v(-38.87, 83.46) * mm, "mid": v(-39.09, 80.36) * mm, "end": v(-39.06, 77.25) * mm});
            skLineSegment(sketch, "E522", {"start": v(-39.06, 77.25) * mm, "end": v(-38.44, 77.25) * mm});
            skArc(sketch, "E523", {"start": v(-38.44, 77.25) * mm, "mid": v(-38.23, 77.26) * mm, "end": v(-38.02, 77.3) * mm});
            skArc(sketch, "E524", {"start": v(-38.02, 77.3) * mm, "mid": v(-37.33, 77.49) * mm, "end": v(-36.64, 77.68) * mm});
            skArc(sketch, "E525", {"start": v(-36.64, 77.68) * mm, "mid": v(-35.83, 77.92) * mm, "end": v(-35.01, 78.16) * mm});
            skArc(sketch, "E526", {"start": v(-35.01, 78.16) * mm, "mid": v(-34.1, 78.44) * mm, "end": v(-33.2, 78.73) * mm});
            skArc(sketch, "E527", {"start": v(-33.2, 78.73) * mm, "mid": v(-32.2, 79.04) * mm, "end": v(-31.22, 79.33) * mm});
            skArc(sketch, "E528", {"start": v(-31.22, 79.33) * mm, "mid": v(-30.17, 79.64) * mm, "end": v(-29.13, 79.93) * mm});
            skArc(sketch, "E529", {"start": v(-29.13, 79.93) * mm, "mid": v(-28.17, 80.19) * mm, "end": v(-27.21, 80.43) * mm});
            skArc(sketch, "E530", {"start": v(-27.21, 80.43) * mm, "mid": v(-25.2, 80.87) * mm, "end": v(-23.17, 81.26) * mm});
            skLineSegment(sketch, "E531", {"start": v(-23.17, 81.26) * mm, "end": v(-22.86, 85.5) * mm});
            skLineSegment(sketch, "E532", {"start": v(-22.86, 85.5) * mm, "end": v(-22.56, 89.75) * mm});
            skLineSegment(sketch, "E533", {"start": v(-22.56, 89.75) * mm, "end": v(-21.06, 89.75) * mm});
            skLineSegment(sketch, "E534", {"start": v(-21.06, 89.75) * mm, "end": v(-19.56, 89.75) * mm});
            skLineSegment(sketch, "E535", {"start": v(-19.56, 89.75) * mm, "end": v(-18.81, 79.25) * mm});
            skArc(sketch, "E536", {"start": v(-18.81, 79.25) * mm, "mid": v(-18.66, 77.2) * mm, "end": v(-18.5, 75.15) * mm});
            skArc(sketch, "E537", {"start": v(-18.5, 75.15) * mm, "mid": v(-18.34, 73.34) * mm, "end": v(-18.17, 71.54) * mm});
            skArc(sketch, "E538", {"start": v(-18.17, 71.54) * mm, "mid": v(-18.02, 70) * mm, "end": v(-17.86, 68.48) * mm});
            skArc(sketch, "E539", {"start": v(-17.86, 68.48) * mm, "mid": v(-17.64, 67.6) * mm, "end": v(-17.31, 66.75) * mm});
            skLineSegment(sketch, "E540", {"start": v(-17.31, 66.75) * mm, "end": v(-0.14, 66.75) * mm});
            skLineSegment(sketch, "E541", {"start": v(-0.14, 66.75) * mm, "end": v(17.03, 66.75) * mm});
            skLineSegment(sketch, "E542", {"start": v(17.03, 66.75) * mm, "end": v(17.52, 68.75) * mm});
            skArc(sketch, "E543", {"start": v(-3.3, -90.03) * mm, "mid": v(-2.57, -89.95) * mm, "end": v(-1.83, -89.9) * mm});
            skArc(sketch, "E544", {"start": v(-1.83, -89.9) * mm, "mid": v(-0.94, -89.87) * mm, "end": v(-0.06, -89.86) * mm});
            skArc(sketch, "E545", {"start": v(-0.06, -89.86) * mm, "mid": v(0.83, -89.87) * mm, "end": v(1.71, -89.9) * mm});
            skArc(sketch, "E546", {"start": v(1.71, -89.9) * mm, "mid": v(4.08, -90.12) * mm, "end": v(6.44, -90.43) * mm});
            skLineSegment(sketch, "E547", {"start": v(6.44, -90.43) * mm, "end": v(-0.06, -90.43) * mm});
            skLineSegment(sketch, "E548", {"start": v(-0.06, -90.43) * mm, "end": v(-6.56, -90.43) * mm});
            skLineSegment(sketch, "E549", {"start": v(-6.56, -90.43) * mm, "end": v(-3.3, -90.03) * mm});
            skLineSegment(sketch, "E550", {"start": v(-53.98, -43.17) * mm, "end": v(-53.9, -41.25) * mm});
            skLineSegment(sketch, "E551", {"start": v(-53.9, -41.25) * mm, "end": v(-53.37, -42.57) * mm});
            skLineSegment(sketch, "E552", {"start": v(-53.37, -42.57) * mm, "end": v(-52.85, -43.88) * mm});
            skLineSegment(sketch, "E553", {"start": v(-52.85, -43.88) * mm, "end": v(-53.45, -44.48) * mm});
            skLineSegment(sketch, "E554", {"start": v(-53.45, -44.48) * mm, "end": v(-54.06, -45.09) * mm});
            skLineSegment(sketch, "E555", {"start": v(-54.06, -45.09) * mm, "end": v(-53.98, -43.17) * mm});
            skLineSegment(sketch, "E556", {"start": v(53.02, -43.17) * mm, "end": v(53.1, -41.25) * mm});
            skLineSegment(sketch, "E557", {"start": v(53.1, -41.25) * mm, "end": v(53.63, -42.57) * mm});
            skLineSegment(sketch, "E558", {"start": v(53.63, -42.57) * mm, "end": v(54.15, -43.88) * mm});
            skLineSegment(sketch, "E559", {"start": v(54.15, -43.88) * mm, "end": v(53.55, -44.48) * mm});
            skLineSegment(sketch, "E560", {"start": v(53.55, -44.48) * mm, "end": v(52.94, -45.09) * mm});
            skLineSegment(sketch, "E561", {"start": v(52.94, -45.09) * mm, "end": v(53.02, -43.17) * mm});
            skLineSegment(sketch, "E562", {"start": v(-54.98, -31.17) * mm, "end": v(-54.9, -29.25) * mm});
            skLineSegment(sketch, "E563", {"start": v(-54.9, -29.25) * mm, "end": v(-54.37, -30.57) * mm});
            skLineSegment(sketch, "E564", {"start": v(-54.37, -30.57) * mm, "end": v(-53.85, -31.88) * mm});
            skLineSegment(sketch, "E565", {"start": v(-53.85, -31.88) * mm, "end": v(-54.45, -32.48) * mm});
            skLineSegment(sketch, "E566", {"start": v(-54.45, -32.48) * mm, "end": v(-55.06, -33.09) * mm});
            skLineSegment(sketch, "E567", {"start": v(-55.06, -33.09) * mm, "end": v(-54.98, -31.17) * mm});
            skLineSegment(sketch, "E568", {"start": v(54.02, -31.17) * mm, "end": v(54.1, -29.25) * mm});
            skLineSegment(sketch, "E569", {"start": v(54.1, -29.25) * mm, "end": v(54.63, -30.57) * mm});
            skLineSegment(sketch, "E570", {"start": v(54.63, -30.57) * mm, "end": v(55.15, -31.88) * mm});
            skLineSegment(sketch, "E571", {"start": v(55.15, -31.88) * mm, "end": v(54.55, -32.48) * mm});
            skLineSegment(sketch, "E572", {"start": v(54.55, -32.48) * mm, "end": v(53.94, -33.09) * mm});
            skLineSegment(sketch, "E573", {"start": v(53.94, -33.09) * mm, "end": v(54.02, -31.17) * mm});
            skLineSegment(sketch, "E574", {"start": v(-16.24, -27.07) * mm, "end": v(-14.93, -26.55) * mm});
            skLineSegment(sketch, "E575", {"start": v(-14.93, -26.55) * mm, "end": v(-14.33, -27.15) * mm});
            skLineSegment(sketch, "E576", {"start": v(-14.33, -27.15) * mm, "end": v(-13.72, -27.75) * mm});
            skLineSegment(sketch, "E577", {"start": v(-13.72, -27.75) * mm, "end": v(-15.64, -27.67) * mm});
            skLineSegment(sketch, "E578", {"start": v(-15.64, -27.67) * mm, "end": v(-17.56, -27.6) * mm});
            skLineSegment(sketch, "E579", {"start": v(-17.56, -27.6) * mm, "end": v(-16.24, -27.07) * mm});
            skArc(sketch, "E580", {"start": v(15.7, -27.05) * mm, "mid": v(16.2, -26.97) * mm, "end": v(16.7, -26.91) * mm});
            skArc(sketch, "E581", {"start": v(16.7, -26.91) * mm, "mid": v(17.26, -26.88) * mm, "end": v(17.81, -26.87) * mm});
            skArc(sketch, "E582", {"start": v(17.81, -26.87) * mm, "mid": v(18.35, -26.89) * mm, "end": v(18.88, -26.92) * mm});
            skArc(sketch, "E583", {"start": v(18.88, -26.92) * mm, "mid": v(20.17, -27.17) * mm, "end": v(21.44, -27.52) * mm});
            skLineSegment(sketch, "E584", {"start": v(21.44, -27.52) * mm, "end": v(17.44, -27.5) * mm});
            skLineSegment(sketch, "E585", {"start": v(17.44, -27.5) * mm, "end": v(13.44, -27.48) * mm});
            skLineSegment(sketch, "E586", {"start": v(13.44, -27.48) * mm, "end": v(15.7, -27.05) * mm});
            skArc(sketch, "E587", {"start": v(-1.3, -19.1) * mm, "mid": v(-1.03, -19) * mm, "end": v(-0.74, -18.94) * mm});
            skArc(sketch, "E588", {"start": v(-0.74, -18.94) * mm, "mid": v(-0.4, -18.9) * mm, "end": v(-0.06, -18.88) * mm});
            skArc(sketch, "E589", {"start": v(-0.06, -18.88) * mm, "mid": v(0.28, -18.9) * mm, "end": v(0.62, -18.94) * mm});
            skArc(sketch, "E590", {"start": v(0.62, -18.94) * mm, "mid": v(1.55, -19.21) * mm, "end": v(2.44, -19.6) * mm});
            skLineSegment(sketch, "E591", {"start": v(2.44, -19.6) * mm, "end": v(-0.06, -19.6) * mm});
            skLineSegment(sketch, "E592", {"start": v(-0.06, -19.6) * mm, "end": v(-2.56, -19.6) * mm});
            skLineSegment(sketch, "E593", {"start": v(-2.56, -19.6) * mm, "end": v(-1.3, -19.1) * mm});
            skLineSegment(sketch, "E594", {"start": v(-58.82, -2.75) * mm, "end": v(-58.82, 0.75) * mm});
            skLineSegment(sketch, "E595", {"start": v(-58.82, 0.75) * mm, "end": v(-58.37, -1) * mm});
            skArc(sketch, "E596", {"start": v(-58.37, -1) * mm, "mid": v(-58.28, -1.4) * mm, "end": v(-58.22, -1.8) * mm});
            skArc(sketch, "E597", {"start": v(-58.22, -1.8) * mm, "mid": v(-58.2, -2.28) * mm, "end": v(-58.18, -2.75) * mm});
            skArc(sketch, "E598", {"start": v(-58.18, -2.75) * mm, "mid": v(-58.2, -3.23) * mm, "end": v(-58.22, -3.7) * mm});
            skArc(sketch, "E599", {"start": v(-58.22, -3.7) * mm, "mid": v(-58.47, -5) * mm, "end": v(-58.82, -6.25) * mm});
            skLineSegment(sketch, "E600", {"start": v(-58.82, -6.25) * mm, "end": v(-58.82, -2.75) * mm});
            skLineSegment(sketch, "E601", {"start": v(58.2, -2.25) * mm, "end": v(58.22, 1.75) * mm});
            skLineSegment(sketch, "E602", {"start": v(58.22, 1.75) * mm, "end": v(58.65, -0.52) * mm});
            skArc(sketch, "E603", {"start": v(58.65, -0.52) * mm, "mid": v(58.73, -1.01) * mm, "end": v(58.78, -1.5) * mm});
            skArc(sketch, "E604", {"start": v(58.78, -1.5) * mm, "mid": v(58.82, -2.07) * mm, "end": v(58.82, -2.62) * mm});
            skArc(sketch, "E605", {"start": v(58.82, -2.62) * mm, "mid": v(58.81, -3.16) * mm, "end": v(58.77, -3.69) * mm});
            skArc(sketch, "E606", {"start": v(58.77, -3.69) * mm, "mid": v(58.53, -4.98) * mm, "end": v(58.18, -6.25) * mm});
            skLineSegment(sketch, "E607", {"start": v(58.18, -6.25) * mm, "end": v(58.2, -2.25) * mm});
            skLineSegment(sketch, "E608", {"start": v(-48.98, -0.17) * mm, "end": v(-48.9, 1.75) * mm});
            skLineSegment(sketch, "E609", {"start": v(-48.9, 1.75) * mm, "end": v(-48.37, 0.43) * mm});
            skLineSegment(sketch, "E610", {"start": v(-48.37, 0.43) * mm, "end": v(-47.85, -0.88) * mm});
            skLineSegment(sketch, "E611", {"start": v(-47.85, -0.88) * mm, "end": v(-48.45, -1.48) * mm});
            skLineSegment(sketch, "E612", {"start": v(-48.45, -1.48) * mm, "end": v(-49.06, -2.09) * mm});
            skLineSegment(sketch, "E613", {"start": v(-49.06, -2.09) * mm, "end": v(-48.98, -0.17) * mm});
            skLineSegment(sketch, "E614", {"start": v(-44.98, 2.83) * mm, "end": v(-44.9, 4.75) * mm});
            skLineSegment(sketch, "E615", {"start": v(-44.9, 4.75) * mm, "end": v(-44.37, 3.43) * mm});
            skLineSegment(sketch, "E616", {"start": v(-44.37, 3.43) * mm, "end": v(-43.85, 2.12) * mm});
            skLineSegment(sketch, "E617", {"start": v(-43.85, 2.12) * mm, "end": v(-44.45, 1.52) * mm});
            skLineSegment(sketch, "E618", {"start": v(-44.45, 1.52) * mm, "end": v(-45.06, 0.91) * mm});
            skLineSegment(sketch, "E619", {"start": v(-45.06, 0.91) * mm, "end": v(-44.98, 2.83) * mm});
            skLineSegment(sketch, "E620", {"start": v(-45.98, 13.83) * mm, "end": v(-45.9, 15.75) * mm});
            skLineSegment(sketch, "E621", {"start": v(-45.9, 15.75) * mm, "end": v(-45.37, 14.43) * mm});
            skLineSegment(sketch, "E622", {"start": v(-45.37, 14.43) * mm, "end": v(-44.85, 13.12) * mm});
            skLineSegment(sketch, "E623", {"start": v(-44.85, 13.12) * mm, "end": v(-45.45, 12.52) * mm});
            skLineSegment(sketch, "E624", {"start": v(-45.45, 12.52) * mm, "end": v(-46.06, 11.91) * mm});
            skLineSegment(sketch, "E625", {"start": v(-46.06, 11.91) * mm, "end": v(-45.98, 13.83) * mm});
            skLineSegment(sketch, "E626", {"start": v(-63.8, 23.75) * mm, "end": v(-63.78, 27.75) * mm});
            skLineSegment(sketch, "E627", {"start": v(-63.78, 27.75) * mm, "end": v(-63.35, 25.48) * mm});
            skArc(sketch, "E628", {"start": v(-63.35, 25.48) * mm, "mid": v(-63.27, 24.99) * mm, "end": v(-63.22, 24.5) * mm});
            skArc(sketch, "E629", {"start": v(-63.22, 24.5) * mm, "mid": v(-63.18, 23.93) * mm, "end": v(-63.18, 23.38) * mm});
            skArc(sketch, "E630", {"start": v(-63.18, 23.38) * mm, "mid": v(-63.19, 22.84) * mm, "end": v(-63.23, 22.31) * mm});
            skArc(sketch, "E631", {"start": v(-63.23, 22.31) * mm, "mid": v(-63.47, 21.02) * mm, "end": v(-63.82, 19.75) * mm});
            skLineSegment(sketch, "E632", {"start": v(-63.82, 19.75) * mm, "end": v(-63.8, 23.75) * mm});
            skLineSegment(sketch, "E633", {"start": v(63.2, 23.75) * mm, "end": v(63.22, 27.75) * mm});
            skLineSegment(sketch, "E634", {"start": v(63.22, 27.75) * mm, "end": v(63.65, 25.48) * mm});
            skArc(sketch, "E635", {"start": v(63.65, 25.48) * mm, "mid": v(63.73, 24.99) * mm, "end": v(63.78, 24.5) * mm});
            skArc(sketch, "E636", {"start": v(63.78, 24.5) * mm, "mid": v(63.82, 23.93) * mm, "end": v(63.82, 23.38) * mm});
            skArc(sketch, "E637", {"start": v(63.82, 23.38) * mm, "mid": v(63.81, 22.84) * mm, "end": v(63.77, 22.31) * mm});
            skArc(sketch, "E638", {"start": v(63.77, 22.31) * mm, "mid": v(63.53, 21.02) * mm, "end": v(63.18, 19.75) * mm});
            skLineSegment(sketch, "E639", {"start": v(63.18, 19.75) * mm, "end": v(63.2, 23.75) * mm});
            skLineSegment(sketch, "E640", {"start": v(-57.86, 36.75) * mm, "end": v(-57.82, 39.75) * mm});
            skLineSegment(sketch, "E641", {"start": v(-57.82, 39.75) * mm, "end": v(-57.36, 37.98) * mm});
            skArc(sketch, "E642", {"start": v(-57.36, 37.98) * mm, "mid": v(-57.28, 37.6) * mm, "end": v(-57.22, 37.2) * mm});
            skArc(sketch, "E643", {"start": v(-57.22, 37.2) * mm, "mid": v(-57.2, 36.79) * mm, "end": v(-57.18, 36.37) * mm});
            skArc(sketch, "E644", {"start": v(-57.18, 36.37) * mm, "mid": v(-57.2, 35.97) * mm, "end": v(-57.24, 35.57) * mm});
            skArc(sketch, "E645", {"start": v(-57.24, 35.57) * mm, "mid": v(-57.51, 34.64) * mm, "end": v(-57.9, 33.75) * mm});
            skLineSegment(sketch, "E646", {"start": v(-57.9, 33.75) * mm, "end": v(-57.86, 36.75) * mm});
            skLineSegment(sketch, "E647", {"start": v(47.02, 36.83) * mm, "end": v(47.1, 38.75) * mm});
            skLineSegment(sketch, "E648", {"start": v(47.1, 38.75) * mm, "end": v(47.63, 37.43) * mm});
            skLineSegment(sketch, "E649", {"start": v(47.63, 37.43) * mm, "end": v(48.15, 36.12) * mm});
            skLineSegment(sketch, "E650", {"start": v(48.15, 36.12) * mm, "end": v(47.55, 35.52) * mm});
            skLineSegment(sketch, "E651", {"start": v(47.55, 35.52) * mm, "end": v(46.94, 34.91) * mm});
            skLineSegment(sketch, "E652", {"start": v(46.94, 34.91) * mm, "end": v(47.02, 36.83) * mm});
            skLineSegment(sketch, "E653", {"start": v(57.14, 37.75) * mm, "end": v(57.18, 40.75) * mm});
            skLineSegment(sketch, "E654", {"start": v(57.18, 40.75) * mm, "end": v(57.64, 38.98) * mm});
            skArc(sketch, "E655", {"start": v(57.64, 38.98) * mm, "mid": v(57.72, 38.6) * mm, "end": v(57.78, 38.2) * mm});
            skArc(sketch, "E656", {"start": v(57.78, 38.2) * mm, "mid": v(57.8, 37.79) * mm, "end": v(57.82, 37.37) * mm});
            skArc(sketch, "E657", {"start": v(57.82, 37.37) * mm, "mid": v(57.8, 36.97) * mm, "end": v(57.76, 36.57) * mm});
            skArc(sketch, "E658", {"start": v(57.76, 36.57) * mm, "mid": v(57.49, 35.64) * mm, "end": v(57.1, 34.75) * mm});
            skLineSegment(sketch, "E659", {"start": v(57.1, 34.75) * mm, "end": v(57.14, 37.75) * mm});
            skLineSegment(sketch, "E660", {"start": v(48.02, 47.83) * mm, "end": v(48.1, 49.75) * mm});
            skLineSegment(sketch, "E661", {"start": v(48.1, 49.75) * mm, "end": v(48.63, 48.43) * mm});
            skLineSegment(sketch, "E662", {"start": v(48.63, 48.43) * mm, "end": v(49.15, 47.12) * mm});
            skLineSegment(sketch, "E663", {"start": v(49.15, 47.12) * mm, "end": v(48.55, 46.52) * mm});
            skLineSegment(sketch, "E664", {"start": v(48.55, 46.52) * mm, "end": v(47.94, 45.91) * mm});
            skLineSegment(sketch, "E665", {"start": v(47.94, 45.91) * mm, "end": v(48.02, 47.83) * mm});
            skLineSegment(sketch, "E666", {"start": v(-57.86, 49.75) * mm, "end": v(-57.82, 52.75) * mm});
            skLineSegment(sketch, "E667", {"start": v(-57.82, 52.75) * mm, "end": v(-57.36, 50.98) * mm});
            skArc(sketch, "E668", {"start": v(-57.36, 50.98) * mm, "mid": v(-57.28, 50.6) * mm, "end": v(-57.22, 50.2) * mm});
            skArc(sketch, "E669", {"start": v(-57.22, 50.2) * mm, "mid": v(-57.2, 49.79) * mm, "end": v(-57.18, 49.37) * mm});
            skArc(sketch, "E670", {"start": v(-57.18, 49.37) * mm, "mid": v(-57.2, 48.97) * mm, "end": v(-57.24, 48.57) * mm});
            skArc(sketch, "E671", {"start": v(-57.24, 48.57) * mm, "mid": v(-57.51, 47.64) * mm, "end": v(-57.9, 46.75) * mm});
            skLineSegment(sketch, "E672", {"start": v(-57.9, 46.75) * mm, "end": v(-57.86, 49.75) * mm});
            skLineSegment(sketch, "E673", {"start": v(57.1, 49.25) * mm, "end": v(57.1, 51.75) * mm});
            skLineSegment(sketch, "E674", {"start": v(57.1, 51.75) * mm, "end": v(57.6, 50.5) * mm});
            skArc(sketch, "E675", {"start": v(57.6, 50.5) * mm, "mid": v(57.7, 50.22) * mm, "end": v(57.76, 49.93) * mm});
            skArc(sketch, "E676", {"start": v(57.76, 49.93) * mm, "mid": v(57.8, 49.59) * mm, "end": v(57.81, 49.25) * mm});
            skArc(sketch, "E677", {"start": v(57.81, 49.25) * mm, "mid": v(57.8, 48.9) * mm, "end": v(57.76, 48.57) * mm});
            skArc(sketch, "E678", {"start": v(57.76, 48.57) * mm, "mid": v(57.48, 47.64) * mm, "end": v(57.1, 46.75) * mm});
            skLineSegment(sketch, "E679", {"start": v(57.1, 46.75) * mm, "end": v(57.1, 49.25) * mm});
            skLineSegment(sketch, "E680", {"start": v(61.02, 53.83) * mm, "end": v(61.1, 55.75) * mm});
            skLineSegment(sketch, "E681", {"start": v(61.1, 55.75) * mm, "end": v(61.63, 54.43) * mm});
            skLineSegment(sketch, "E682", {"start": v(61.63, 54.43) * mm, "end": v(62.15, 53.12) * mm});
            skLineSegment(sketch, "E683", {"start": v(62.15, 53.12) * mm, "end": v(61.55, 52.52) * mm});
            skLineSegment(sketch, "E684", {"start": v(61.55, 52.52) * mm, "end": v(60.94, 51.91) * mm});
            skLineSegment(sketch, "E685", {"start": v(60.94, 51.91) * mm, "end": v(61.02, 53.83) * mm});
            skLineSegment(sketch, "E686", {"start": v(-9.24, 62.93) * mm, "end": v(-7.93, 63.45) * mm});
            skLineSegment(sketch, "E687", {"start": v(-7.93, 63.45) * mm, "end": v(-7.33, 62.85) * mm});
            skLineSegment(sketch, "E688", {"start": v(-7.33, 62.85) * mm, "end": v(-6.72, 62.25) * mm});
            skLineSegment(sketch, "E689", {"start": v(-6.72, 62.25) * mm, "end": v(-8.64, 62.33) * mm});
            skLineSegment(sketch, "E690", {"start": v(-8.64, 62.33) * mm, "end": v(-10.56, 62.4) * mm});
            skLineSegment(sketch, "E691", {"start": v(-10.56, 62.4) * mm, "end": v(-9.24, 62.93) * mm});
            skLineSegment(sketch, "E692", {"start": v(7.76, 62.93) * mm, "end": v(9.07, 63.45) * mm});
            skLineSegment(sketch, "E693", {"start": v(9.07, 63.45) * mm, "end": v(9.67, 62.85) * mm});
            skLineSegment(sketch, "E694", {"start": v(9.67, 62.85) * mm, "end": v(10.28, 62.25) * mm});
            skLineSegment(sketch, "E695", {"start": v(10.28, 62.25) * mm, "end": v(8.36, 62.33) * mm});
            skLineSegment(sketch, "E696", {"start": v(8.36, 62.33) * mm, "end": v(6.44, 62.4) * mm});
            skLineSegment(sketch, "E697", {"start": v(6.44, 62.4) * mm, "end": v(7.76, 62.93) * mm});
            skLineSegment(sketch, "E698", {"start": v(46.87, 70) * mm, "end": v(44.44, 72.75) * mm});
            skLineSegment(sketch, "E699", {"start": v(44.44, 72.75) * mm, "end": v(47.2, 70.32) * mm});
            skArc(sketch, "E700", {"start": v(47.2, 70.32) * mm, "mid": v(47.72, 69.85) * mm, "end": v(48.25, 69.37) * mm});
            skArc(sketch, "E701", {"start": v(48.25, 69.37) * mm, "mid": v(48.7, 68.95) * mm, "end": v(49.14, 68.51) * mm});
            skArc(sketch, "E702", {"start": v(49.14, 68.51) * mm, "mid": v(49.5, 68.15) * mm, "end": v(49.86, 67.77) * mm});
            skArc(sketch, "E703", {"start": v(49.86, 67.77) * mm, "mid": v(49.95, 67.52) * mm, "end": v(49.94, 67.25) * mm});
            skLineSegment(sketch, "E704", {"start": v(49.94, 67.25) * mm, "end": v(49.62, 67.25) * mm});
            skArc(sketch, "E705", {"start": v(49.62, 67.25) * mm, "mid": v(49.5, 67.27) * mm, "end": v(49.42, 67.33) * mm});
            skArc(sketch, "E706", {"start": v(49.42, 67.33) * mm, "mid": v(49.04, 67.69) * mm, "end": v(48.68, 68.05) * mm});
            skArc(sketch, "E707", {"start": v(48.68, 68.05) * mm, "mid": v(48.24, 68.5) * mm, "end": v(47.82, 68.94) * mm});
            skArc(sketch, "E708", {"start": v(47.82, 68.94) * mm, "mid": v(47.34, 69.47) * mm, "end": v(46.87, 70) * mm});
            skArc(sketch, "E709", {"start": v(21.94, 75.15) * mm, "mid": v(21.96, 75.36) * mm, "end": v(22.02, 75.57) * mm});
            skArc(sketch, "E710", {"start": v(22.02, 75.57) * mm, "mid": v(22.13, 75.8) * mm, "end": v(22.26, 76.03) * mm});
            skArc(sketch, "E711", {"start": v(22.26, 76.03) * mm, "mid": v(22.42, 76.26) * mm, "end": v(22.6, 76.46) * mm});
            skArc(sketch, "E712", {"start": v(22.6, 76.46) * mm, "mid": v(23.31, 77) * mm, "end": v(24.08, 77.45) * mm});
            skLineSegment(sketch, "E713", {"start": v(24.08, 77.45) * mm, "end": v(24.4, 77.1) * mm});
            skLineSegment(sketch, "E714", {"start": v(24.4, 77.1) * mm, "end": v(24.74, 76.75) * mm});
            skLineSegment(sketch, "E715", {"start": v(24.74, 76.75) * mm, "end": v(23.34, 75.46) * mm});
            skLineSegment(sketch, "E716", {"start": v(23.34, 75.46) * mm, "end": v(21.94, 74.17) * mm});
            skLineSegment(sketch, "E717", {"start": v(21.94, 74.17) * mm, "end": v(21.94, 75.15) * mm});
            skLineSegment(sketch, "E718", {"start": v(-38.78, 81.25) * mm, "end": v(-38.78, 85.75) * mm});
            skLineSegment(sketch, "E719", {"start": v(-38.78, 85.75) * mm, "end": v(-38.35, 83.5) * mm});
            skArc(sketch, "E720", {"start": v(-38.35, 83.5) * mm, "mid": v(-38.27, 82.99) * mm, "end": v(-38.22, 82.47) * mm});
            skArc(sketch, "E721", {"start": v(-38.22, 82.47) * mm, "mid": v(-38.18, 81.86) * mm, "end": v(-38.17, 81.25) * mm});
            skArc(sketch, "E722", {"start": v(-38.17, 81.25) * mm, "mid": v(-38.18, 80.63) * mm, "end": v(-38.22, 80.02) * mm});
            skArc(sketch, "E723", {"start": v(-38.22, 80.02) * mm, "mid": v(-38.45, 78.37) * mm, "end": v(-38.78, 76.75) * mm});
            skLineSegment(sketch, "E724", {"start": v(-38.78, 76.75) * mm, "end": v(-38.78, 81.25) * mm});
            skLineSegment(sketch, "E725", {"start": v(38.2, 80.75) * mm, "end": v(38.22, 84.75) * mm});
            skLineSegment(sketch, "E726", {"start": v(38.22, 84.75) * mm, "end": v(38.65, 82.48) * mm});
            skArc(sketch, "E727", {"start": v(38.65, 82.48) * mm, "mid": v(38.73, 81.99) * mm, "end": v(38.78, 81.5) * mm});
            skArc(sketch, "E728", {"start": v(38.78, 81.5) * mm, "mid": v(38.82, 80.93) * mm, "end": v(38.82, 80.38) * mm});
            skArc(sketch, "E729", {"start": v(38.82, 80.38) * mm, "mid": v(38.81, 79.84) * mm, "end": v(38.77, 79.31) * mm});
            skArc(sketch, "E730", {"start": v(38.77, 79.31) * mm, "mid": v(38.53, 78.02) * mm, "end": v(38.18, 76.75) * mm});
            skLineSegment(sketch, "E731", {"start": v(38.18, 76.75) * mm, "end": v(38.2, 80.75) * mm});
            skSolve(sketch);
        }
        {
            var Q0;
            Q0=makeQuery(id+"F6.imprint","IMPRINT",FACE,{"disambiguationData":[TD([[makeQuery(id+"F6.imprint","IMPRINT",EDGE,{"derivedFrom":sQuery(id+"F6.wireOp",EDGE,"E7")}),-1.0]])]});
            var Q1;
            {var subQ0=sQuery(id+"F6.wireOp",EDGE,"E610");Q1=makeQuery(id+"F6.imprint","IMPRINT",FACE,{"disambiguationData":[TD([[makeQuery(id+"F6.imprint","IMPRINT",EDGE,{"derivedFrom":subQ0}),-1.0]])]});}
            var Q2;
            {var subQ1=sQuery(id+"F6.wireOp",EDGE,"E614");Q2=makeQuery(id+"F6.imprint","IMPRINT",FACE,{"disambiguationData":[TD([[makeQuery(id+"F6.imprint","IMPRINT",EDGE,{"derivedFrom":subQ1}),-1.0]])]});}
            var Q3;
            {var subQ0=sQuery(id+"F6.wireOp",EDGE,"E553");var subQ1=sQuery(id+"F6.wireOp",EDGE,"E13");var subQ2=makeQuery(id+"F6.imprint","INTERSECT",VERTEX,{"derivedFrom":[subQ1,subQ0]});Q3=makeQuery(id+"F6.imprint","IMPRINT",FACE,{"disambiguationData":[TD([[makeQuery(id+"F6.imprint","IMPRINT",EDGE,{"disambiguationData":[TD([[subQ2,-1.0]])],"derivedFrom":subQ1}),-1.0]])]});}
            var Q4;
            {var subQ5=sQuery(id+"F6.wireOp",EDGE,"E564");Q4=makeQuery(id+"F6.imprint","IMPRINT",FACE,{"disambiguationData":[TD([[makeQuery(id+"F6.imprint","IMPRINT",EDGE,{"derivedFrom":subQ5}),-1.0]])]});}
            var Q5;
            {var subQ5=sQuery(id+"F6.wireOp",EDGE,"E568");Q5=makeQuery(id+"F6.imprint","IMPRINT",FACE,{"disambiguationData":[TD([[makeQuery(id+"F6.imprint","IMPRINT",EDGE,{"derivedFrom":subQ5}),-1.0]])]});}
            var Q6;
            {var subQ5=sQuery(id+"F6.wireOp",EDGE,"E650");Q6=makeQuery(id+"F6.imprint","IMPRINT",FACE,{"disambiguationData":[TD([[makeQuery(id+"F6.imprint","IMPRINT",EDGE,{"derivedFrom":subQ5}),-1.0]])]});}
            var Q7;
            {var subQ5=sQuery(id+"F6.wireOp",EDGE,"E663");Q7=makeQuery(id+"F6.imprint","IMPRINT",FACE,{"disambiguationData":[TD([[makeQuery(id+"F6.imprint","IMPRINT",EDGE,{"derivedFrom":subQ5}),-1.0]])]});}
            var Q8;
            {var subQ0=sQuery(id+"F6.wireOp",EDGE,"E675");Q8=makeQuery(id+"F6.imprint","IMPRINT",FACE,{"disambiguationData":[TD([[makeQuery(id+"F6.imprint","IMPRINT",EDGE,{"derivedFrom":subQ0}),-1.0]])]});}
            var Q9;
            {var subQ5=sQuery(id+"F6.wireOp",EDGE,"E685");Q9=makeQuery(id+"F6.imprint","IMPRINT",FACE,{"disambiguationData":[TD([[makeQuery(id+"F6.imprint","IMPRINT",EDGE,{"derivedFrom":subQ5}),-1.0]])]});}
            var Q10;
            {var subQ1=sQuery(id+"F6.wireOp",EDGE,"E713");Q10=makeQuery(id+"F6.imprint","IMPRINT",FACE,{"disambiguationData":[TD([[makeQuery(id+"F6.imprint","IMPRINT",EDGE,{"derivedFrom":subQ1}),-1.0]])]});}
            var Q11;
            Q11=makeQuery(id+"F6.imprint","IMPRINT",FACE,{"disambiguationData":[TD([[makeQuery(id+"F6.imprint","IMPRINT",EDGE,{"derivedFrom":sQuery(id+"F6.wireOp",EDGE,"E709")}),-1.0]])]});
            var Q12;
            {var subQ4=sQuery(id+"F6.wireOp",EDGE,"E692");Q12=makeQuery(id+"F6.imprint","IMPRINT",FACE,{"disambiguationData":[TD([[makeQuery(id+"F6.imprint","IMPRINT",EDGE,{"derivedFrom":subQ4}),-1.0]])]});}
            var Q13;
            {var subQ1=sQuery(id+"F6.wireOp",EDGE,"E686");Q13=makeQuery(id+"F6.imprint","IMPRINT",FACE,{"disambiguationData":[TD([[makeQuery(id+"F6.imprint","IMPRINT",EDGE,{"derivedFrom":subQ1}),-1.0]])]});}
            var Q14;
            {var subQ1=sQuery(id+"F6.wireOp",EDGE,"E666");Q14=makeQuery(id+"F6.imprint","IMPRINT",FACE,{"disambiguationData":[TD([[makeQuery(id+"F6.imprint","IMPRINT",EDGE,{"derivedFrom":subQ1}),-1.0]])]});}
            extrude(context, id + "F7", {"entities" : qUnion([Q0, Q1, Q2, Q3, Q4, Q5, Q6, Q7, Q8, Q9, Q10, Q11, Q12, Q13, Q14]), "operationType" : NewBodyOperationType.ADD, "depth" : 5 * mm, "offsetDistance" : 25 * mm});
        }
        {
            var Q0;
            Q0=qCreatedBy(makeId("Right.planeOp"),FACE);
            var sketch = newSketch(context, id + "F8", { "sketchPlane" : qUnion([Q0])});
            skLineSegment(sketch, "E732", {"start": v(-105.8, 0.42) * mm, "end": v(-107.73, -1.88) * mm});
            skLineSegment(sketch, "E733", {"start": v(-108.45, 6.33) * mm, "end": v(-107.73, -1.88) * mm});
            skLineSegment(sketch, "E734", {"start": v(-106.15, 4.4) * mm, "end": v(-108.45, 6.33) * mm});
            skLineSegment(sketch, "E735.right", {"start": v(-106.15, 4.4) * mm, "end": v(-105.8, 0.42) * mm});
            skLineSegment(sketch, "E736", {"start": v(-106.1, 3.9) * mm, "end": v(-99.1, 3.9) * mm});
            skLineSegment(sketch, "E737", {"start": v(-99.1, 3.9) * mm, "end": v(-99.1, 0.92) * mm});
            skLineSegment(sketch, "E738", {"start": v(-99.1, 0.92) * mm, "end": v(-105.85, 0.92) * mm});
            skLineSegment(sketch, "E739", {"start": v(-105.8, 0.42) * mm, "end": v(-105.85, 0.92) * mm});
            skLineSegment(sketch, "E740", {"start": v(-106.15, 4.4) * mm, "end": v(-106.1, 3.9) * mm});
            skSolve(sketch);
        }
        {
            var Q0;
            Q0=makeQuery(id+"F8.imprint","IMPRINT",FACE,{"disambiguationData":[TD([[makeQuery(id+"F8.imprint","IMPRINT",EDGE,{"derivedFrom":sQuery(id+"F8.wireOp",EDGE,"E735.right")}),1.0]])]});
            var Q1;
            Q1=makeQuery(id+"F8.imprint","IMPRINT",FACE,{"disambiguationData":[TD([[makeQuery(id+"F8.imprint","IMPRINT",EDGE,{"derivedFrom":sQuery(id+"F8.wireOp",EDGE,"E732")}),-1.0]])]});
            extrude(context, id + "F9", {"entities" : qUnion([Q0, Q1]), "operationType" : NewBodyOperationType.REMOVE, "flatOperationType" : FlatOperationType.REMOVE, "endBound" : BoundingType.SYMMETRIC, "depth" : 160 * mm, "offsetDistance" : 25 * mm, "domain" : OperationDomain.MODEL});
        }
    });
